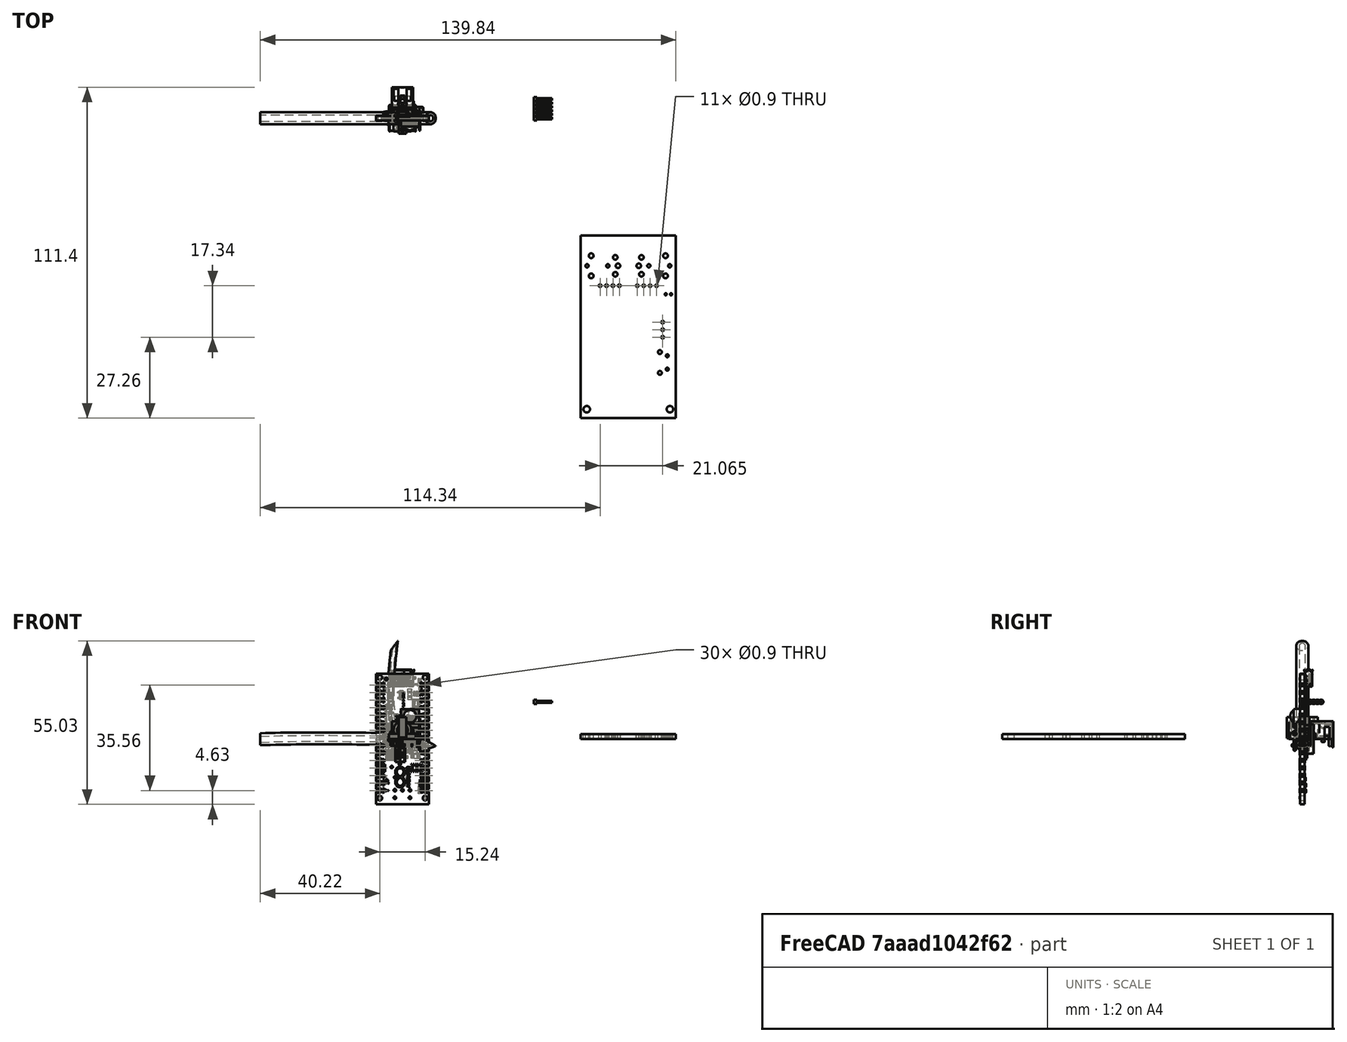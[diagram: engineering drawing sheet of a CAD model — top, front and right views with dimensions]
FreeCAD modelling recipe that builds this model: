
FCSTD DOCUMENT  (FreeCAD 0.21R33694 (Git))
Label: mainboard_step
License: All rights reserved
LicenseURL: http://en.wikipedia.org/wiki/All_rights_reserved
objects: Part::Feature×109, App::Part×72, Sketcher::SketchObject×23, PartDesign::Pad×7, PartDesign::Body×6, Part::Sweep×6, App::VRMLObject×6, Mesh::Feature×5, Image::ImagePlane×3, PartDesign::AdditivePipe×2
note: 162 computed .brp shape members not serialized (recipe doc carries the construction recipe); baked Part::Feature solids carry a one-line shape summary decoded from their .brp

FEATURE [Part::Feature] Part__Feature  label="SOLID"
  shape: bbox 1.6 x 0.8 x 0.8 mm, 28 faces (baked)
FEATURE [App::Part] C_0603_1608Metric
  Group = -> [Part__Feature]
  Origin = -> Origin
  Placement = pos=(70.4,-42.375,1.65) rot=(0,0,1;3.14159rad)
FEATURE [Part::Feature] Part__Feature001  label="SOLID001"
  shape: bbox 2.8 x 3 x 4.75 mm, 48 faces (baked)
FEATURE [App::Part] SFH4045N
  Group = -> [Part__Feature001]
  Origin = -> Origin001
  Placement = pos=(66.4,-99.3,2.24) rot=(0.57735,-0.57735,0.57735;2.0944rad)
FEATURE [Part::Feature] Part__Feature002  label="SOLID002"
  shape: bbox 2.506 x 2.463 x 1.1 mm, 67 faces (baked)
FEATURE [App::Part] D_SOD_323  label="D_SOD-323"
  Group = -> [Part__Feature002]
  Origin = -> Origin002
  Placement = pos=(74,-42.4,1.65) rot=(0,0,1;0rad)
FEATURE [Part::Feature] Part__Feature003  label="SOLID003"
  shape: bbox 1.6 x 0.8 x 0.45 mm, 26 faces (baked)
FEATURE [App::Part] R_0603_1608Metric
  Group = -> [Part__Feature003]
  Origin = -> Origin003
  Placement = pos=(86,-92.9,1.65) rot=(0,0,1;0rad)
FEATURE [Part::Feature] Part__Feature006  label="SOLID005"
  shape: bbox 1.6 x 0.8 x 0.8 mm, 28 faces (baked)
FEATURE [App::Part] C_0603_1608Metric001
  Group = -> [Part__Feature006]
  Origin = -> Origin006
  Placement = pos=(81.6,-42.4,1.65) rot=(0,0,1;0rad)
FEATURE [Part::Feature] Part__Feature008  label="SOLID007"
  shape: bbox 2.506 x 2.463 x 1.1 mm, 67 faces (baked)
FEATURE [App::Part] D_SOD_323001  label="D_SOD-324"
  Group = -> [Part__Feature008]
  Origin = -> Origin008
  Placement = pos=(78,-42.4,1.65) rot=(0,0,1;3.14159rad)
FEATURE [Part::Feature] Part__Feature010  label="SOLID008"
  shape: bbox 1.6 x 0.8 x 0.45 mm, 26 faces (baked)
FEATURE [App::Part] R_0603_1608Metric001
  Group = -> [Part__Feature010]
  Origin = -> Origin010
  Placement = pos=(82.7,-93.9,1.65) rot=(0,0,1;1.5708rad)
FEATURE [Part::Feature] Part__Feature011  label="SOLID009"
  shape: bbox 7.4 x 9.9 x 11 mm, 130 faces (baked)
FEATURE [App::Part] SW_Tactile_SPST_Angled_PTS645Vx58_2LFS  label="SW_Tactile_SPST_Angled_PTS645Vx58-2LFS"
  Group = -> [Part__Feature011]
  Origin = -> Origin011
  Placement = pos=(89.1,-80,1.9) rot=(0,0,-1;1.5708rad)
FEATURE [Part::Feature] Part__Feature012  label="SOLID010"
  shape: bbox 1.6 x 0.8 x 0.8 mm, 28 faces (baked)
FEATURE [App::Part] C_0603_1608Metric002
  Group = -> [Part__Feature012]
  Origin = -> Origin012
  Placement = pos=(71.2,-70.662,1.65) rot=(0,0,1;1.5708rad)
FEATURE [Part::Feature] Part__Feature013  label="SOLID011"
  shape: bbox 2.8 x 3 x 4.75 mm, 48 faces (baked)
FEATURE [App::Part] SFH4045N001
  Group = -> [Part__Feature013]
  Origin = -> Origin013
  Placement = pos=(90.3,-94,2.24) rot=(0.707107,0,0.707107;3.14159rad)
FEATURE [Part::Feature] Part__Feature014  label="SOLID012"
  shape: bbox 1.6 x 0.8 x 0.45 mm, 26 faces (baked)
FEATURE [App::Part] R_0603_1608Metric002
  Group = -> [Part__Feature014]
  Origin = -> Origin014
  Placement = pos=(82.7,-97.1,1.65) rot=(0,0,1;1.5708rad)
FEATURE [Part::Feature] Part__Feature015  label="SOLID013"
  shape: bbox 2.8 x 3 x 4.75 mm, 48 faces (baked)
FEATURE [App::Part] SFH4045N002
  Group = -> [Part__Feature015]
  Origin = -> Origin015
  Placement = pos=(85.6,-99.3,2.24) rot=(0.57735,-0.57735,0.57735;2.0944rad)
FEATURE [Part::Feature] Part__Feature017  label="COMPOUND003"
  shape: bbox 9.637 x 7.014 x 5.767 mm, 553 faces, 8 solids (baked)
FEATURE [App::Part] _90367280676  label="690367280676_wrl"
  Group = -> [Part__Feature017]
  Origin = -> Origin017
  Placement = pos=(75.965,-84.05,4.15) rot=(0,0,1;0rad)
FEATURE [Part::Feature] Part__Feature018  label="SOLID014"
  shape: bbox 2.8 x 3 x 4.75 mm, 48 faces (baked)
FEATURE [App::Part] SFH4045N003
  Group = -> [Part__Feature018]
  Origin = -> Origin018
  Placement = pos=(61.681,-93.2,2.24) rot=(0,-1,0;1.5708rad)
FEATURE [Part::Feature] Part__Feature020  label="SOLID015"
  shape: bbox 9 x 9 x 1.9 mm, 41 faces (baked)
FEATURE [App::Part] Buzzer_Murata_PKMCS0909E4000_R1  label="Buzzer_Murata_PKMCS0909E4000-R1"
  Group = -> [Part__Feature020]
  Origin = -> Origin020
  Placement = pos=(76.4,-62.9,1.65) rot=(0,0,1;3.14159rad)
FEATURE [Part::Feature] Part__Feature021  label="SOLID016"
  shape: bbox 3.18 x 3.679 x 1.2 mm, 76 faces (baked)
FEATURE [App::Part] SOT_23  label="SOT-23"
  Group = -> [Part__Feature021]
  Origin = -> Origin021
  Placement = pos=(86.4,-89.85,1.65) rot=(0,0,1;0rad)
FEATURE [Part::Feature] Part__Feature022  label="SOLID017"
  shape: bbox 1.6 x 0.8 x 0.8 mm, 28 faces (baked)
FEATURE [App::Part] C_0603_1608Metric003
  Group = -> [Part__Feature022]
  Origin = -> Origin022
  Placement = pos=(80.79,-70.69,1.65) rot=(0,0,1;1.5708rad)
FEATURE [Part::Feature] Part__Feature023  label="SOLID018"
  shape: bbox 3.2 x 2.5 x 2.5 mm, 28 faces (baked)
FEATURE [App::Part] C_1210_3225Metric
  Group = -> [Part__Feature023]
  Origin = -> Origin023
  Placement = pos=(82.6,-89.9,1.65) rot=(0,0,1;1.5708rad)
FEATURE [Part::Feature] Part__Feature024  label="SOLID019"
  shape: bbox 4.776 x 10.36 x 7.4 mm, 150 faces (baked)
FEATURE [App::Part] PinSocket_1x04_P2_54mm_Vertical_SMD_Pin1Right  label="PinSocket_1x04_P2.54mm_Vertical_SMD_Pin1Right"
  Group = -> [Part__Feature024]
  Origin = -> Origin024
  Placement = pos=(76,-97.1,1.65) rot=(0,0,-1;1.5708rad)
FEATURE [Part::Feature] Part__Feature025  label="SOLID020"
  shape: bbox 6 x 7.908 x 13.34 mm, 75 faces (baked)
FEATURE [App::Part] Vishay_MOLD_3Pin  label="Vishay_MOLD-3Pin"
  Group = -> [Part__Feature025]
  Origin = -> Origin025
  Placement = pos=(87.565,-73.74,0.15) rot=(0,0,1;1.5708rad)
FEATURE [Part::Feature] Part__Feature026  label="COMPOUND005"
  shape: bbox 5.019 x 5.033 x 5.871 mm, 347 faces, 24 solids (baked)
FEATURE [App::Part] Honeywell_MPRL
  Group = -> [Part__Feature026]
  Origin = -> Origin026
  Placement = pos=(76,-70.662,1.65) rot=(0,0,1;0rad)
FEATURE [Part::Feature] Part__Feature028  label="FM3_mainboard PCB"
  shape: bbox 32 x 61.5 x 1.6 mm, 39 faces (baked)
FEATURE [Image::ImagePlane] ImagePlane
  Placement = pos=(76.25,-70,3e-16) rot=(0,1,0;3.14159rad)
  XSize = 32
  YSize = 61.5
FEATURE [Image::ImagePlane] ImagePlane001
  Placement = pos=(76,-70.25,1.75) rot=(0,0,1;0rad)
  XSize = 32
  YSize = 61.5
FEATURE [Part::Feature] Part__Feature029  label="Nano_33IoT Body"
  shape: bbox 17.78 x 1.75 x 44 mm, 2561 faces (baked)
FEATURE [Part::Feature] Part__Feature030  label="User Library-arduino_nano_reset core"
  shape: bbox 5.209 x 2.159 x 2.809 mm, 76 faces (baked)
FEATURE [Part::Feature] Part__Feature031  label="User Library-arduino_nano_reset shell"
  Placement = pos=(0,1.65,0) rot=(0,-1,0;1.5708rad)
  shape: bbox 4 x 1.65 x 3 mm, 71 faces (baked)
FEATURE [App::Part] Reser_Button  label="Reser Button"
  Group = -> [Part__Feature030,Part__Feature031]
  Origin = -> Origin030
  Placement = pos=(4.5e-15,0.8,10.91) rot=(0,0,1;0rad)
FEATURE [Part::Feature] Part__Feature032  label="atmegaSAMD21"
  Placement = pos=(-1.21,0.82,-0.24) rot=(0,1,0;1.5708rad)
  shape: bbox 7.242 x 1.032 x 7.242 mm, 984 faces (baked)
FEATURE [Part::Feature] Part__Feature033  label="HSMG-C190 LED"
  Placement = pos=(5.79,0.8,19.6) rot=(0,-1,0;1.5708rad)
  shape: bbox 0.8 x 0.8 x 1.6 mm, 18 faces (baked)
FEATURE [Part::Feature] Part__Feature034  label="HSMG-C190 LED001"
  Placement = pos=(-5.81,0.8,20.1) rot=(0,-1,0;1.5708rad)
  shape: bbox 0.8 x 0.8 x 1.6 mm, 18 faces (baked)
FEATURE [Part::Feature] Part__Feature035  label="ZX62-AB-5PA Micro USB"
  Placement = pos=(0,2.22,19.2) rot=(0,0,1;0rad)
  shape: bbox 8.814 x 3.085 x 5.639 mm, 871 faces (baked)
FEATURE [Part::Feature] Part__Feature036  label="LSM6DS3 Accelerometer"
  Placement = pos=(4.6275,0.82,12) rot=(0,1,0;3.14159rad)
  shape: bbox 2.5 x 0.85 x 3 mm, 190 faces (baked)
FEATURE [Part::Feature] Part__Feature037  label="MPM3610 Step-Down Module"
  Placement = pos=(3.69,1.65,6.25) rot=(0,-1,0;1.5708rad)
  shape: bbox 5.15 x 1.65 x 3.3 mm, 330 faces (baked)
FEATURE [Part::Feature] Part__Feature038  label="NINA-W102 Body"
  shape: bbox 14 x 0.85 x 10 mm, 250 faces (baked)
FEATURE [Part::Feature] Part__Feature039  label="NINA-W102 Antenna"
  Placement = pos=(7,0.8,2e-15) rot=(0,0,1;0rad)
  shape: bbox 3.8 x 3 x 10 mm, 99 faces (baked)
FEATURE [Part::Feature] Part__Feature040  label="NINA-W102 Cover"
  Placement = pos=(-1.7,2,0) rot=(0,-1,0;1.5708rad)
  shape: bbox 9.6 x 1.45 x 9.5 mm, 75 faces (baked)
FEATURE [App::Part] NINA_W102_Module  label="NINA-W102 Module"
  Group = -> [Part__Feature038,Part__Feature039,Part__Feature040]
  Origin = -> Origin031
  Placement = pos=(2.17e-14,0.85,-14.5) rot=(0,1,0;1.5708rad)
FEATURE [Part::Feature] Part__Feature041  label="ATECC608A No Lead Crypto Auth"
  Placement = pos=(-4.035,0.8,-6.08) rot=(0,1,0;1.5708rad)
  shape: bbox 3.3 x 0.55 x 2 mm, 213 faces (baked)
FEATURE [Part::Feature] Part__Feature042  label="CL21A226MQCLQNC Capacitor"
  Placement = pos=(4.44,1.225,-5.85) rot=(0,1,0;3.14159rad)
  shape: bbox 3 x 0.8705 x 1.25 mm, 52 faces (baked)
FEATURE [Part::Feature] Part__Feature043  label="TDK C1005 Capacitor"
  Placement = pos=(5.5825,1.05,-15.55) rot=(0,1,0;1.5708rad)
  shape: bbox 0.5 x 0.5165 x 1.8 mm, 46 faces (baked)
FEATURE [Part::Feature] Part__Feature044  label="TDK C1005 Capacitor001"
  Placement = pos=(5.5825,1.05,-17.5125) rot=(0,1,0;1.5708rad)
  shape: bbox 0.5 x 0.5165 x 1.8 mm, 46 faces (baked)
FEATURE [Part::Feature] Part__Feature045  label="CL21A226MQCLQNC Capacitor001"
  Placement = pos=(-4.11,1.225,7.8375) rot=(0,-1,0;1.5708rad)
  shape: bbox 1.25 x 0.8705 x 3 mm, 52 faces (baked)
FEATURE [Part::Feature] Part__Feature046  label="TDK C1005 Capacitor002"
  Placement = pos=(5.385,1.05,15.7375) rot=(0,0,1;0rad)
  shape: bbox 1.8 x 0.5165 x 0.5 mm, 46 faces (baked)
FEATURE [Part::Feature] Part__Feature047  label="TDK C1005 Capacitor003"
  Placement = pos=(5.385,1.05,14.7625) rot=(0,0,1;0rad)
  shape: bbox 1.8 x 0.5165 x 0.5 mm, 46 faces (baked)
FEATURE [Part::Feature] Part__Feature048  label="PRTR5V0U2X Protection Diode"
  Placement = pos=(-0.41,1.45,14.77) rot=(0,1,0;1.5708rad)
  shape: bbox 2.5 x 1.1 x 3 mm, 139 faces (baked)
FEATURE [Part::Feature] Part__Feature049  label="PMEG6020AELR Diode"
  Placement = pos=(-4.06,0.85,14.1) rot=(0,-1,0;1.5708rad)
  shape: bbox 1.9 x 1.11 x 3.3 mm, 80 faces (baked)
FEATURE [Part::Feature] Part__Feature050  label="C0805C472KDRACTU Capacitor"
  Placement = pos=(2.415,1.425,15.1325) rot=(0,-1,0;1.5708rad)
  shape: bbox 1.25 x 1.301 x 3.5 mm, 52 faces (baked)
FEATURE [Part::Feature] Part__Feature051  label="TDK C1005 Capacitor004"
  Placement = pos=(-1.52,1.05,-6.46) rot=(0,1,0;1.5708rad)
  shape: bbox 0.5 x 0.5165 x 1.8 mm, 46 faces (baked)
FEATURE [Part::Feature] Part__Feature052  label="BLM18PG471SN1D Ferrite Bead"
  Placement = pos=(0.61,1.2,-6.1) rot=(0,1,0;3.14159rad)
  shape: bbox 2.5 x 0.8142 x 0.8 mm, 52 faces (baked)
FEATURE [Part::Feature] Part__Feature053  label="TDK C1005 Capacitor005"
  Placement = pos=(-5.66,1.05,-4.35) rot=(0,1,0;3.14159rad)
  shape: bbox 1.8 x 0.5165 x 0.5 mm, 46 faces (baked)
FEATURE [Part::Feature] Part__Feature054  label="TDK C1005 Capacitor006"
  Placement = pos=(-3.64,1.05,10.73) rot=(0,-1,0;1.5708rad)
  shape: bbox 0.5 x 0.5165 x 1.8 mm, 46 faces (baked)
FEATURE [Part::Feature] Part__Feature055  label="TDK C1005 Capacitor007"
  Placement = pos=(-3.79,1.05,5.1) rot=(0,0,1;0rad)
  shape: bbox 1.8 x 0.5165 x 0.5 mm, 46 faces (baked)
FEATURE [Part::Feature] Part__Feature056  label="GRM188R61E475KE11D Capacitor"
  Placement = pos=(-5.59,1.2,4.4) rot=(0,-1,0;1.5708rad)
  shape: bbox 0.8 x 0.8142 x 2.5 mm, 52 faces (baked)
FEATURE [Part::Feature] Part__Feature057  label="RC0402FR-07100KL Resistor"
  Placement = pos=(-2.01,1,8.1625) rot=(0,1,0;3.14159rad)
  shape: bbox 1.47 x 0.4379 x 0.5 mm, 68 faces (baked)
FEATURE [Part::Feature] Part__Feature058  label="RC0402FR-07100KL Resistor001"
  Placement = pos=(-1.6975,1,6.7125) rot=(0,-1,0;1.5708rad)
  shape: bbox 0.5 x 0.4379 x 1.47 mm, 68 faces (baked)
FEATURE [Part::Feature] Part__Feature059  label="RC0402FR-07330RL Resistor"
  Placement = pos=(-5.81,1,16.6) rot=(0,-1,0;1.5708rad)
  shape: bbox 0.5 x 0.4379 x 1.47 mm, 68 faces (baked)
FEATURE [Part::Feature] Part__Feature060  label="RC0402FR-07330RL Resistor001"
  Placement = pos=(5.8025,1,17.2) rot=(0,-1,0;1.5708rad)
  shape: bbox 0.5 x 0.4379 x 1.47 mm, 68 faces (baked)
FEATURE [Part::Feature] Part__Feature061  label="RC0402FR-07330RL Resistor002"
  Placement = pos=(3.915,1,15.2325) rot=(0,-1,0;1.5708rad)
  shape: bbox 0.5 x 0.4379 x 1.47 mm, 68 faces (baked)
FEATURE [Part::Feature] Part__Feature062  label="TDK C1005 Capacitor008"
  Placement = pos=(5.09,1.05,3.1) rot=(0,1,0;3.14159rad)
  shape: bbox 1.8 x 0.5165 x 0.5 mm, 46 faces (baked)
FEATURE [Part::Feature] Part__Feature063  label="RC0402FR-074K7L Resistor"
  Placement = pos=(5.09,1,2.1) rot=(0,0,1;0rad)
  shape: bbox 1.47 x 0.4379 x 0.5 mm, 68 faces (baked)
FEATURE [Part::Feature] Part__Feature064  label="RC0402FR-074K7L Resistor001"
  Placement = pos=(5.09,1,1.1) rot=(0,1,0;3.14159rad)
  shape: bbox 1.47 x 0.4379 x 0.5 mm, 68 faces (baked)
FEATURE [Part::Feature] Part__Feature065  label="GRM155R61E105KA12D Capacitor"
  Placement = pos=(5.09,1.05,0.1) rot=(0,0,1;0rad)
  shape: bbox 1.8 x 0.5165 x 0.5 mm, 46 faces (baked)
FEATURE [Part::Feature] Part__Feature066  label="TDK C1005 Capacitor009"
  Placement = pos=(5.09,1.05,-0.9) rot=(0,1,0;3.14159rad)
  shape: bbox 1.8 x 0.5165 x 0.5 mm, 46 faces (baked)
FEATURE [Part::Feature] Part__Feature067  label="RC0402FR-071KL Resistor"
  Placement = pos=(5.09,1,-1.9) rot=(0,1,0;3.14159rad)
  shape: bbox 1.47 x 0.4379 x 0.5 mm, 68 faces (baked)
FEATURE [Part::Feature] Part__Feature068  label="RC0402FR-07100KL Resistor002"
  Placement = pos=(-5.74,1,-13.5) rot=(0,1,0;1.5708rad)
  shape: bbox 0.5 x 0.4379 x 1.47 mm, 68 faces (baked)
FEATURE [Part::Feature] Part__Feature069  label="RC0402FR-07100KL Resistor003"
  Placement = pos=(-4.64,1,10.73) rot=(0,-1,0;1.5708rad)
  shape: bbox 0.5 x 0.4379 x 1.47 mm, 68 faces (baked)
FEATURE [Part::Feature] Part__Feature070  label="AC0402JR-0724KL Resistor"
  Placement = pos=(4.665,0.985,9.725) rot=(0,0,1;0rad)
  shape: bbox 1.47 x 0.4079 x 0.5 mm, 68 faces (baked)
FEATURE [Part::Feature] Part__Feature071  label="AC0402JR-0775KL Resistor"
  Placement = pos=(4.665,0.985,8.725) rot=(0,0,1;0rad)
  shape: bbox 1.47 x 0.4079 x 0.5 mm, 68 faces (baked)
FEATURE [App::Part] Arduino_Nano_33_IoT  label="Arduino Nano 33 IoT"
  Group = -> [Part__Feature029,Reser_Button,Part__Feature032,Part__Feature033,Part__Feature034,Part__Feature035,Part__Feature036,Part__Feature037,NINA_W102_Module,Part__Feature041,Part__Feature042,Part__Feature043,Part__Feature044,Part__Feature045,Part__Feature046,Part__Feature047,Part__Feature048,Part__Feature049,Part__Feature050,Part__Feature051,Part__Feature052,Part__Feature053,Part__Feature054,+17 more]
  Origin = -> Origin032
FEATURE [App::Part] ArduinoNanoRP2040
  Group = -> [Arduino_Nano_33_IoT]
  Origin = -> Origin027
  Placement = pos=(73.4,-78.1,-0.05) rot=(0,0.707107,-0.707107;3.14159rad)
FEATURE [Part::Feature] Part__Feature072  label="Telo konektora"
  shape: bbox 7 x 14.9 x 7.247 mm, 88 faces (baked)
FEATURE [Part::Feature] Part__Feature073  label="Kontakt most"
  shape: bbox 7.472 x 8.966 x 8.306 mm, 60 faces (baked)
FEATURE [Part::Feature] Part__Feature074  label="Kontakt 1"
  shape: bbox 6 x 4 x 8.5 mm, 26 faces, 2 solids (baked)
FEATURE [Part::Feature] Part__Feature075  label="Kontakt 2"
  shape: bbox 1 x 0.3 x 3 mm, 8 faces (baked)
FEATURE [App::Part] Audio_konektor_FC68125_3_5_mm_v5  label="Audio konektor FC68125 3.5 mm v5"
  Group = -> [Part__Feature072,Part__Feature073,Part__Feature074,Part__Feature075]
  Origin = -> Origin033
FEATURE [App::Part] FC68125
  Group = -> [Audio_konektor_FC68125_3_5_mm_v5]
  Origin = -> Origin004
  Placement = pos=(62.4,-49.7,1.65) rot=(0,0,-1;1.5708rad)
FEATURE [Part::Feature] Part__Feature076  label="Telo konektora001"
  shape: bbox 7 x 14.9 x 7.247 mm, 88 faces (baked)
FEATURE [Part::Feature] Part__Feature077  label="Kontakt most001"
  shape: bbox 7.472 x 8.966 x 8.306 mm, 60 faces (baked)
FEATURE [Part::Feature] Part__Feature078  label="Kontakt 003"
  shape: bbox 6 x 4 x 8.5 mm, 26 faces, 2 solids (baked)
FEATURE [Part::Feature] Part__Feature079  label="Kontakt 004"
  shape: bbox 1 x 0.3 x 3 mm, 8 faces (baked)
FEATURE [App::Part] Audio_konektor_FC68125_3_5_mm_v006  label="Audio konektor FC68125 3.5 mm v006"
  Group = -> [Part__Feature076,Part__Feature077,Part__Feature078,Part__Feature079]
  Origin = -> Origin034
FEATURE [App::Part] FC68125001
  Group = -> [Audio_konektor_FC68125_3_5_mm_v006]
  Origin = -> Origin016
  Placement = pos=(89.6,-49.7,1.65) rot=(0,0,1;1.5708rad)
FEATURE [Mesh::Feature] np_led_bendlegs
FEATURE [App::Part] LED_D5_0mm_Horizontal_O3_81mm_Z9_0mm001  label="LED_D5.0mm_Horizontal_O3.81mm_Z9.0mm001"
  Group = -> [np_led_bendlegs]
  Origin = -> Origin007
  Placement = pos=(68.5,-55.9,13.9) rot=(1,0,0;3.14159rad)
FEATURE [Mesh::Feature] np_led_bendlegs001
FEATURE [App::Part] LED_D5_0mm_Horizontal_O3_81mm_Z9_0mm  label="LED_D5.0mm_Horizontal_O3.81mm_Z9.0mm"
  Group = -> [np_led_bendlegs001]
  Origin = -> Origin005
  Placement = pos=(81.023,-55.9,13.9) rot=(-1,0,0;3.14159rad)
FEATURE [Mesh::Feature] FM3_case_lid  label="FM3_case-lid"
FEATURE [Sketcher::SketchObject] Sketch
  FullyConstrained = false
  MapMode = 5
  Placement = pos=(0,0,0) rot=(0.57735,0.57735,0.57735;2.0944rad)
  sketch-geometry (23):
    g0: LineSegment StartX=0 StartY=0 StartZ=0 EndX=1.27335 EndY=0 EndZ=0
    g1: LineSegment StartX=0 StartY=0 StartZ=0 EndX=1.27103 EndY=0 EndZ=0
    g2: LineSegment StartX=1.27103 StartY=0 StartZ=0 EndX=2.54207 EndY=0 EndZ=0
    g3: LineSegment StartX=2.54207 StartY=0 StartZ=0 EndX=3.8131 EndY=0 EndZ=0
    g4: LineSegment StartX=3.8131 StartY=0 StartZ=0 EndX=5.08414 EndY=0 EndZ=0
    g5: LineSegment StartX=0.45 StartY=0.6 StartZ=0 EndX=0.821034 EndY=0.6 EndZ=0
    g6: LineSegment StartX=0.45 StartY=-0.6 StartZ=0 EndX=0.821034 EndY=-0.6 EndZ=0
    g7: ArcOfCircle CenterX=5.08414 CenterY=7.1e-15 CenterZ=0 NormalX=0 NormalY=0 NormalZ=1 AngleXU=0 Radius=0.75 StartAngle=4.06889 EndAngle=5.35589
    g8: ArcOfCircle CenterX=3.8131 CenterY=0 CenterZ=0 NormalX=0 NormalY=0 NormalZ=1 AngleXU=0 Radius=0.75 StartAngle=4.06889 EndAngle=5.35589
    g9: ArcOfCircle CenterX=2.54207 CenterY=0 CenterZ=0 NormalX=0 NormalY=0 NormalZ=1 AngleXU=0 Radius=0.75 StartAngle=4.06889 EndAngle=5.35589
    g10: ArcOfCircle CenterX=1.27103 CenterY=-2e-16 CenterZ=0 NormalX=0 NormalY=0 NormalZ=1 AngleXU=0 Radius=0.75 StartAngle=4.06889 EndAngle=5.35589
    g11: ArcOfCircle CenterX=0 CenterY=-1e-16 CenterZ=0 NormalX=0 NormalY=0 NormalZ=1 AngleXU=0 Radius=0.75 StartAngle=0.927295 EndAngle=5.35589
    g12: ArcOfCircle CenterX=1.27103 CenterY=0 CenterZ=0 NormalX=0 NormalY=0 NormalZ=1 AngleXU=0 Radius=0.75 StartAngle=0.927295 EndAngle=2.2143
    g13: ArcOfCircle CenterX=2.54207 CenterY=0 CenterZ=0 NormalX=0 NormalY=0 NormalZ=1 AngleXU=0 Radius=0.75 StartAngle=0.927295 EndAngle=2.2143
    g14: ArcOfCircle CenterX=3.8131 CenterY=0 CenterZ=0 NormalX=0 NormalY=0 NormalZ=1 AngleXU=0 Radius=0.75 StartAngle=0.927295 EndAngle=2.2143
    g15: ArcOfCircle CenterX=5.08414 CenterY=-9.81007e-08 CenterZ=0 NormalX=0 NormalY=0 NormalZ=1 AngleXU=0 Radius=0.75 StartAngle=0.927295 EndAngle=2.2143
    g16: LineSegment StartX=4.2631 StartY=0.6 StartZ=0 EndX=4.63414 EndY=0.6 EndZ=0
    g17: LineSegment StartX=2.99207 StartY=0.6 StartZ=0 EndX=3.3631 EndY=0.6 EndZ=0
    g18: LineSegment StartX=1.72103 StartY=0.6 StartZ=0 EndX=2.09207 EndY=0.6 EndZ=0
    g19: LineSegment StartX=1.72103 StartY=-0.6 StartZ=0 EndX=2.09207 EndY=-0.6 EndZ=0
    g20: LineSegment StartX=2.99207 StartY=-0.6 StartZ=0 EndX=3.3631 EndY=-0.6 EndZ=0
    g21: LineSegment StartX=4.2631 StartY=-0.6 StartZ=0 EndX=4.63414 EndY=-0.6 EndZ=0
    g22: ArcOfCircle CenterX=5.08414 CenterY=7.1e-15 CenterZ=0 NormalX=0 NormalY=0 NormalZ=1 AngleXU=0 Radius=0.75 StartAngle=5.35589 EndAngle=7.21048
  constraints (36):
    c: Angle(g0) = 0
    c: Distance(g1) = 1.27103
    c: Angle(g1) = 0
    c: Equal(g1,g2)
    c: Parallel(g2,g1)
    c: Equal(g1,g3)
    c: Parallel(g3,g1)
    c: Equal(g1,g4)
    c: Parallel(g4,g1)
    c: Horizontal(g5)
    c: Horizontal(g6)
    c: PointOnObject(g7,g6)
    c: PointOnObject(g7,g6)
    c: PointOnObject(g8,g6)
    c: PointOnObject(g8,g6)
    c: PointOnObject(g9,g6)
    c: PointOnObject(g9,g6)
    c: Coincident(g6,g11)
    c: Coincident(g11,g5)
    c: Coincident(g16,g15)
    c: Coincident(g17,g14)
    c: Coincident(g16,g14)
    c: Coincident(g18,g13)
    c: Coincident(g17,g13)
    c: Coincident(g5,g12)
    c: Coincident(g18,g12)
    c: Coincident(g6,g10)
    c: Coincident(g19,g10)
    c: PointOnObject(g19,g9)
    c: PointOnObject(g20,g9)
    c: PointOnObject(g20,g8)
    c: PointOnObject(g21,g8)
    c: PointOnObject(g21,g7)
    c: Coincident(g22,g7)
    c: Coincident(g22,g15)
    c: Coincident(g22,g7)
FEATURE [Sketcher::SketchObject] Sketch001
  FullyConstrained = false
  MapMode = 5
  Placement = pos=(0,0,0) rot=(0.57735,0.57735,0.57735;2.0944rad)
  Support = -> [YZ_Plane061]
  sketch-geometry (11):
    g0: Circle CenterX=0 CenterY=0 CenterZ=0 NormalX=0 NormalY=0 NormalZ=1 AngleXU=0 Radius=0.340608
    g1: Circle CenterX=1.26883 CenterY=0 CenterZ=0 NormalX=0 NormalY=0 NormalZ=1 AngleXU=0 Radius=0.340608
    g2: LineSegment StartX=0 StartY=0 StartZ=0 EndX=1.26883 EndY=0 EndZ=0
    g3: Circle CenterX=2.53767 CenterY=0 CenterZ=0 NormalX=0 NormalY=0 NormalZ=1 AngleXU=0 Radius=0.340608
    g4: LineSegment StartX=1.26883 StartY=0 StartZ=0 EndX=2.53767 EndY=0 EndZ=0
    g5: Circle CenterX=3.8065 CenterY=0 CenterZ=0 NormalX=0 NormalY=0 NormalZ=1 AngleXU=0 Radius=0.340608
    g6: LineSegment StartX=2.53767 StartY=0 StartZ=0 EndX=3.8065 EndY=0 EndZ=0
    g7: Circle CenterX=5.07533 CenterY=0 CenterZ=0 NormalX=0 NormalY=0 NormalZ=1 AngleXU=0 Radius=0.340608
    g8: LineSegment StartX=3.8065 StartY=0 StartZ=0 EndX=5.07533 EndY=0 EndZ=0
    g9: Circle CenterX=6.34417 CenterY=0 CenterZ=0 NormalX=0 NormalY=0 NormalZ=1 AngleXU=0 Radius=0.340608
    g10: LineSegment StartX=5.07533 StartY=0 StartZ=0 EndX=6.34417 EndY=0 EndZ=0
  constraints (21):
    c: Coincident(g0,g-1)
    c: Coincident(g0,g2)
    c: Coincident(g1,g2)
    c: Distance(g2) = 1.26883
    c: Angle(g2) = 0
    c: Coincident(g1,g4)
    c: Coincident(g3,g4)
    c: Equal(g2,g4)
    c: Parallel(g4,g2)
    c: Coincident(g3,g6)
    c: Coincident(g5,g6)
    c: Equal(g2,g6)
    c: Parallel(g6,g2)
    c: Coincident(g5,g8)
    c: Coincident(g7,g8)
    c: Equal(g2,g8)
    c: Parallel(g8,g2)
    c: Coincident(g7,g10)
    c: Coincident(g9,g10)
    c: Equal(g2,g10)
    c: Parallel(g10,g2)
FEATURE [Sketcher::SketchObject] Sketch003
  FullyConstrained = false
  MapMode = 5
  Placement = pos=(0,0,0) rot=(1,0,0;1.5708rad)
  sketch-geometry (11):
    g0-g5: Circle x6 (B-spline internal-alignment scaffolding for g6; pole/knot coordinates omitted)
    g6: BSplineCurve PolesCount=6 KnotsCount=4 Degree=3 IsPeriodic=0
    g7-g10: GeomPoint x4 (B-spline internal-alignment scaffolding for g6; pole/knot coordinates omitted)
  constraints (4):
    c: Weight(g0) = 1
    c: Equal(g0, g1-g5) x5
    c: InternalAlignment(g0-g5 -> g6) x6
    c: InternalAlignment(g7-g10 -> g6) x4
FEATURE [Sketcher::SketchObject] Sketch004
  FullyConstrained = false
  MapMode = 5
  Placement = pos=(0,0,0) rot=(0.57735,0.57735,0.57735;2.0944rad)
  sketch-geometry (26):
    g0: LineSegment StartX=0 StartY=0 StartZ=0 EndX=1.27335 EndY=0 EndZ=0
    g1: LineSegment StartX=0 StartY=0 StartZ=0 EndX=1.27103 EndY=0 EndZ=0
    g2: LineSegment StartX=1.27103 StartY=0 StartZ=0 EndX=2.54207 EndY=0 EndZ=0
    g3: LineSegment StartX=2.54207 StartY=0 StartZ=0 EndX=3.8131 EndY=0 EndZ=0
    g4: LineSegment StartX=3.8131 StartY=0 StartZ=0 EndX=5.08414 EndY=0 EndZ=0
    g5: ArcOfCircle CenterX=6.35517 CenterY=0 CenterZ=0 NormalX=0 NormalY=0 NormalZ=1 AngleXU=0 Radius=0.75 StartAngle=4.06889 EndAngle=8.49748
    g6: LineSegment StartX=5.08414 StartY=0 StartZ=0 EndX=6.35517 EndY=0 EndZ=0
    g7: LineSegment StartX=0.45 StartY=0.6 StartZ=0 EndX=0.821034 EndY=0.6 EndZ=0
    g8: LineSegment StartX=0.45 StartY=-0.6 StartZ=0 EndX=0.821034 EndY=-0.6 EndZ=0
    g9: ArcOfCircle CenterX=5.08414 CenterY=0 CenterZ=0 NormalX=0 NormalY=0 NormalZ=1 AngleXU=0 Radius=0.75 StartAngle=4.06889 EndAngle=5.35589
    g10: ArcOfCircle CenterX=3.8131 CenterY=0 CenterZ=0 NormalX=0 NormalY=0 NormalZ=1 AngleXU=0 Radius=0.75 StartAngle=4.06889 EndAngle=5.35589
    g11: ArcOfCircle CenterX=2.54207 CenterY=0 CenterZ=0 NormalX=0 NormalY=0 NormalZ=1 AngleXU=0 Radius=0.75 StartAngle=4.06889 EndAngle=5.35589
    g12: ArcOfCircle CenterX=1.27103 CenterY=0 CenterZ=0 NormalX=0 NormalY=0 NormalZ=1 AngleXU=0 Radius=0.75 StartAngle=4.06889 EndAngle=5.35589
    g13: ArcOfCircle CenterX=0 CenterY=0 CenterZ=0 NormalX=0 NormalY=0 NormalZ=1 AngleXU=0 Radius=0.75 StartAngle=0.927295 EndAngle=5.35589
    g14: ArcOfCircle CenterX=1.27103 CenterY=0 CenterZ=0 NormalX=0 NormalY=0 NormalZ=1 AngleXU=0 Radius=0.75 StartAngle=0.927295 EndAngle=2.2143
    g15: ArcOfCircle CenterX=2.54207 CenterY=0 CenterZ=0 NormalX=0 NormalY=0 NormalZ=1 AngleXU=0 Radius=0.75 StartAngle=0.927295 EndAngle=2.2143
    g16: ArcOfCircle CenterX=3.8131 CenterY=0 CenterZ=0 NormalX=0 NormalY=0 NormalZ=1 AngleXU=0 Radius=0.75 StartAngle=0.927295 EndAngle=2.2143
    g17: ArcOfCircle CenterX=5.08414 CenterY=0 CenterZ=0 NormalX=0 NormalY=0 NormalZ=1 AngleXU=0 Radius=0.75 StartAngle=0.927295 EndAngle=2.2143
    g18: LineSegment StartX=5.53414 StartY=0.6 StartZ=0 EndX=5.90517 EndY=0.6 EndZ=0
    g19: LineSegment StartX=4.2631 StartY=0.6 StartZ=0 EndX=4.63414 EndY=0.6 EndZ=0
    g20: LineSegment StartX=2.99207 StartY=0.6 StartZ=0 EndX=3.3631 EndY=0.6 EndZ=0
    g21: LineSegment StartX=1.72103 StartY=0.6 StartZ=0 EndX=2.09207 EndY=0.6 EndZ=0
    g22: LineSegment StartX=1.72103 StartY=-0.6 StartZ=0 EndX=2.09207 EndY=-0.6 EndZ=0
    g23: LineSegment StartX=2.99207 StartY=-0.6 StartZ=0 EndX=3.3631 EndY=-0.6 EndZ=0
    g24: LineSegment StartX=4.2631 StartY=-0.6 StartZ=0 EndX=4.63414 EndY=-0.6 EndZ=0
    g25: LineSegment StartX=5.53414 StartY=-0.6 StartZ=0 EndX=5.90517 EndY=-0.6 EndZ=0
  constraints (41):
    c: Angle(g0) = 0
    c: Distance(g1) = 1.27103
    c: Angle(g1) = 0
    c: Equal(g1,g2)
    c: Parallel(g2,g1)
    c: Equal(g1,g3)
    c: Parallel(g3,g1)
    c: Equal(g1,g4)
    c: Parallel(g4,g1)
    c: Radius(g5) = 0.75
    c: Coincident(g5,g6)
    c: Equal(g1,g6)
    c: Parallel(g6,g1)
    c: Horizontal(g7)
    c: Horizontal(g8)
    c: Coincident(g5,g25)
    c: PointOnObject(g9,g8)
    c: PointOnObject(g9,g8)
    c: PointOnObject(g10,g8)
    c: PointOnObject(g10,g8)
    c: PointOnObject(g11,g8)
    c: PointOnObject(g11,g8)
    c: Coincident(g8,g13)
    c: Coincident(g13,g7)
    c: Coincident(g18,g5)
    c: Coincident(g19,g17)
    c: Coincident(g18,g17)
    c: Coincident(g20,g16)
    c: Coincident(g19,g16)
    c: Coincident(g21,g15)
    c: Coincident(g20,g15)
    c: Coincident(g7,g14)
    c: Coincident(g21,g14)
    c: Coincident(g8,g12)
    c: Coincident(g22,g12)
    c: PointOnObject(g22,g11)
    c: PointOnObject(g23,g11)
    c: PointOnObject(g23,g10)
    c: PointOnObject(g24,g10)
    c: PointOnObject(g24,g9)
    c: PointOnObject(g25,g9)
FEATURE [PartDesign::Pad] Pad
  Direction = (1,0,0)
  Length = 1
  Length2 = 10
  Placement = pos=(0,0,0) rot=(0.57735,0.57735,0.57735;2.0944rad)
  Profile = -> Sketch004
  ReferenceAxis = -> Sketch004 [N_Axis]
  Type = 0
FEATURE [PartDesign::Pad] Pad001
  BaseFeature = -> Pad
  Direction = (1,-2e-16,3e-16)
  Length = 6
  Length2 = 10
  Placement = pos=(0,0,0) rot=(0.57735,0.57735,0.57735;2.0944rad)
  Profile = -> Sketch001
  ReferenceAxis = -> Sketch001 [N_Axis]
  Type = 0
FEATURE [PartDesign::Body] Body001
  Group = -> [Sketch001,Sketch004,Pad,Pad001]
  Origin = -> Origin061
  Placement = pos=(44.25,0,12.5) rot=(0,0,1;0rad)
  Tip = -> Pad001
FEATURE [Sketcher::SketchObject] Sketch005
  FullyConstrained = false
  MapMode = 5
  Placement = pos=(0,0,0) rot=(0.57735,0.57735,0.57735;2.0944rad)
  sketch-geometry (2):
    g0: ArcOfCircle CenterX=6.35517 CenterY=-2.69756e-08 CenterZ=0 NormalX=0 NormalY=0 NormalZ=1 AngleXU=0 Radius=0.75 StartAngle=4.06889 EndAngle=8.49748
    g1: ArcOfCircle CenterX=6.35517 CenterY=-2.69756e-08 CenterZ=0 NormalX=0 NormalY=0 NormalZ=1 AngleXU=0 Radius=0.75 StartAngle=2.2143 EndAngle=4.06889
  constraints (4):
    c: Radius(g0) = 0.75
    c: Coincident(g1,g0)
    c: Coincident(g1,g0)
    c: Coincident(g1,g0)
FEATURE [Sketcher::SketchObject] Sketch006
  FullyConstrained = false
  MapMode = 5
  Placement = pos=(0,0,0) rot=(1,0,0;1.5708rad)
  sketch-geometry (11):
    g0-g5: Circle x6 (B-spline internal-alignment scaffolding for g6; pole/knot coordinates omitted)
    g6: BSplineCurve PolesCount=6 KnotsCount=4 Degree=3 IsPeriodic=0
    g7-g10: GeomPoint x4 (B-spline internal-alignment scaffolding for g6; pole/knot coordinates omitted)
  constraints (4):
    c: Weight(g0) = 1
    c: Equal(g0, g1-g5) x5
    c: InternalAlignment(g0-g5 -> g6) x6
    c: InternalAlignment(g7-g10 -> g6) x4
FEATURE [Part::Sweep] Sweep
  Frenet = false
  Sections = -> [Sketch]
  Solid = false
  Spine = -> Sketch003 [Edge1]
  Transition = 1
FEATURE [Part::Sweep] Sweep001
  Frenet = false
  Sections = -> [Sketch005]
  Solid = false
  Spine = -> Sketch006 [Edge1]
  Transition = 1
FEATURE [App::Part] Part003  label="idc-cable_mounted"
  Group = -> [Body001,Sketch003,Sketch,Sweep,Sketch005,Sketch006,Sweep001]
  Origin = -> Origin062
  Placement = pos=(-3,-1.25,50.25) rot=(-0.57735,-0.57735,0.57735;4.18879rad)
FEATURE [App::VRMLObject] _90157000672001  label="690157000672001"
FEATURE [App::Part] Part004  label="idc-plug_mounted"
  Group = -> [_90157000672001]
  Origin = -> Origin063
  Placement = pos=(-2.18e-14,-0.5,53) rot=(1,0,0;4.71239rad)
FEATURE [Sketcher::SketchObject] Sketch007
  FullyConstrained = true
  MapMode = 5
  Placement = pos=(0,0,0) rot=(0.57735,0.57735,0.57735;2.0944rad)
  Support = -> [YZ_Plane066]
  sketch-geometry (2):
    g0: Circle CenterX=0 CenterY=0 CenterZ=0 NormalX=0 NormalY=0 NormalZ=1 AngleXU=0 Radius=2
    g1: Circle CenterX=0 CenterY=0 CenterZ=0 NormalX=0 NormalY=0 NormalZ=1 AngleXU=0 Radius=3
  constraints (4):
    c: Coincident(g0,g-1)
    c: Radius(g0) = 2
    c: Coincident(g1,g0)
    c: Radius(g1) = 3
FEATURE [PartDesign::Pad] Pad002
  Direction = (1,-2e-16,3e-16)
  Length = 5
  Length2 = 10
  Placement = pos=(0,0,0) rot=(0.57735,0.57735,0.57735;2.0944rad)
  Profile = -> Sketch007
  ReferenceAxis = -> Sketch007 [N_Axis]
  Type = 0
FEATURE [PartDesign::Body] Body  label="4x6_5mm"
  Group = -> [Sketch007,Pad002]
  Origin = -> Origin066
  Tip = -> Pad002
FEATURE [Sketcher::SketchObject] Sketch008  label="diameter"
  FullyConstrained = true
  MapMode = 5
  Placement = pos=(0,0,0) rot=(0.57735,0.57735,0.57735;2.0944rad)
  Support = -> [YZ_Plane067]
  sketch-geometry (2):
    g0: Circle CenterX=0 CenterY=0 CenterZ=0 NormalX=0 NormalY=0 NormalZ=1 AngleXU=0 Radius=1
    g1: Circle CenterX=0 CenterY=0 CenterZ=0 NormalX=0 NormalY=0 NormalZ=1 AngleXU=0 Radius=2
  constraints (4):
    c: Coincident(g0,g-1)
    c: Radius(g0) = 1
    c: Coincident(g1,g0)
    c: Radius(g1) = 2
FEATURE [Sketcher::SketchObject] Sketch009  label="sweep"
  FullyConstrained = false
  MapMode = 5
  Placement = pos=(0,0,0) rot=(1,0,0;1.5708rad)
  Support = -> [XZ_Plane067]
  sketch-geometry (7):
    g0-g3: Circle x4 (B-spline internal-alignment scaffolding for g4; pole/knot coordinates omitted)
    g4: BSplineCurve PolesCount=4 KnotsCount=2 Degree=3 IsPeriodic=0
    g5: GeomPoint X=5.97738 Y=0.542931 Z=0
    g6: GeomPoint X=-0.39634 Y=34.6329 Z=0
  constraints (7):
    c: Weight(g0) = 1
    c: Equal(g0,g1)
    c: Equal(g0,g2)
    c: Equal(g0,g3)
    c: InternalAlignment(g0-g3 -> g4) x4
    c: InternalAlignment(g5,g4)
    c: InternalAlignment(g6,g4)
FEATURE [Sketcher::SketchObject] Sketch010
  FullyConstrained = false
  MapMode = 5
  Placement = pos=(0,0,0) rot=(0.57735,0.57735,0.57735;2.0944rad)
  sketch-geometry (23):
    g0: LineSegment StartX=0 StartY=0 StartZ=0 EndX=1.27335 EndY=0 EndZ=0
    g1: LineSegment StartX=0 StartY=0 StartZ=0 EndX=1.27103 EndY=0 EndZ=0
    g2: LineSegment StartX=1.27103 StartY=0 StartZ=0 EndX=2.54207 EndY=0 EndZ=0
    g3: LineSegment StartX=2.54207 StartY=0 StartZ=0 EndX=3.8131 EndY=0 EndZ=0
    g4: LineSegment StartX=3.8131 StartY=0 StartZ=0 EndX=5.08414 EndY=0 EndZ=0
    g5: LineSegment StartX=0.45 StartY=0.6 StartZ=0 EndX=0.821034 EndY=0.6 EndZ=0
    g6: LineSegment StartX=0.45 StartY=-0.6 StartZ=0 EndX=0.821034 EndY=-0.6 EndZ=0
    g7: ArcOfCircle CenterX=5.08414 CenterY=7.1e-15 CenterZ=0 NormalX=0 NormalY=0 NormalZ=1 AngleXU=0 Radius=0.75 StartAngle=4.06889 EndAngle=5.35589
    g8: ArcOfCircle CenterX=3.8131 CenterY=0 CenterZ=0 NormalX=0 NormalY=0 NormalZ=1 AngleXU=0 Radius=0.75 StartAngle=4.06889 EndAngle=5.35589
    g9: ArcOfCircle CenterX=2.54207 CenterY=0 CenterZ=0 NormalX=0 NormalY=0 NormalZ=1 AngleXU=0 Radius=0.75 StartAngle=4.06889 EndAngle=5.35589
    g10: ArcOfCircle CenterX=1.27103 CenterY=-2e-16 CenterZ=0 NormalX=0 NormalY=0 NormalZ=1 AngleXU=0 Radius=0.75 StartAngle=4.06889 EndAngle=5.35589
    g11: ArcOfCircle CenterX=0 CenterY=-1e-16 CenterZ=0 NormalX=0 NormalY=0 NormalZ=1 AngleXU=0 Radius=0.75 StartAngle=0.927295 EndAngle=5.35589
    g12: ArcOfCircle CenterX=1.27103 CenterY=0 CenterZ=0 NormalX=0 NormalY=0 NormalZ=1 AngleXU=0 Radius=0.75 StartAngle=0.927295 EndAngle=2.2143
    g13: ArcOfCircle CenterX=2.54207 CenterY=0 CenterZ=0 NormalX=0 NormalY=0 NormalZ=1 AngleXU=0 Radius=0.75 StartAngle=0.927295 EndAngle=2.2143
    g14: ArcOfCircle CenterX=3.8131 CenterY=0 CenterZ=0 NormalX=0 NormalY=0 NormalZ=1 AngleXU=0 Radius=0.75 StartAngle=0.927295 EndAngle=2.2143
    g15: ArcOfCircle CenterX=5.08414 CenterY=-9.81007e-08 CenterZ=0 NormalX=0 NormalY=0 NormalZ=1 AngleXU=0 Radius=0.75 StartAngle=0.927295 EndAngle=2.2143
    g16: LineSegment StartX=4.2631 StartY=0.6 StartZ=0 EndX=4.63414 EndY=0.6 EndZ=0
    g17: LineSegment StartX=2.99207 StartY=0.6 StartZ=0 EndX=3.3631 EndY=0.6 EndZ=0
    g18: LineSegment StartX=1.72103 StartY=0.6 StartZ=0 EndX=2.09207 EndY=0.6 EndZ=0
    g19: LineSegment StartX=1.72103 StartY=-0.6 StartZ=0 EndX=2.09207 EndY=-0.6 EndZ=0
    g20: LineSegment StartX=2.99207 StartY=-0.6 StartZ=0 EndX=3.3631 EndY=-0.6 EndZ=0
    g21: LineSegment StartX=4.2631 StartY=-0.6 StartZ=0 EndX=4.63414 EndY=-0.6 EndZ=0
    g22: ArcOfCircle CenterX=5.08414 CenterY=7.1e-15 CenterZ=0 NormalX=0 NormalY=0 NormalZ=1 AngleXU=0 Radius=0.75 StartAngle=5.35589 EndAngle=7.21048
  constraints (36):
    c: Angle(g0) = 0
    c: Distance(g1) = 1.27103
    c: Angle(g1) = 0
    c: Equal(g1,g2)
    c: Parallel(g2,g1)
    c: Equal(g1,g3)
    c: Parallel(g3,g1)
    c: Equal(g1,g4)
    c: Parallel(g4,g1)
    c: Horizontal(g5)
    c: Horizontal(g6)
    c: PointOnObject(g7,g6)
    c: PointOnObject(g7,g6)
    c: PointOnObject(g8,g6)
    c: PointOnObject(g8,g6)
    c: PointOnObject(g9,g6)
    c: PointOnObject(g9,g6)
    c: Coincident(g6,g11)
    c: Coincident(g11,g5)
    c: Coincident(g16,g15)
    c: Coincident(g17,g14)
    c: Coincident(g16,g14)
    c: Coincident(g18,g13)
    c: Coincident(g17,g13)
    c: Coincident(g5,g12)
    c: Coincident(g18,g12)
    c: Coincident(g6,g10)
    c: Coincident(g19,g10)
    c: PointOnObject(g19,g9)
    c: PointOnObject(g20,g9)
    c: PointOnObject(g20,g8)
    c: PointOnObject(g21,g8)
    c: PointOnObject(g21,g7)
    c: Coincident(g22,g7)
    c: Coincident(g22,g15)
    c: Coincident(g22,g7)
FEATURE [Sketcher::SketchObject] Sketch011
  FullyConstrained = false
  MapMode = 5
  Placement = pos=(0,0,0) rot=(0.57735,0.57735,0.57735;2.0944rad)
  Support = -> [YZ_Plane068]
  sketch-geometry (11):
    g0: Circle CenterX=0 CenterY=0 CenterZ=0 NormalX=0 NormalY=0 NormalZ=1 AngleXU=0 Radius=0.340608
    g1: Circle CenterX=1.26883 CenterY=0 CenterZ=0 NormalX=0 NormalY=0 NormalZ=1 AngleXU=0 Radius=0.340608
    g2: LineSegment StartX=0 StartY=0 StartZ=0 EndX=1.26883 EndY=0 EndZ=0
    g3: Circle CenterX=2.53767 CenterY=0 CenterZ=0 NormalX=0 NormalY=0 NormalZ=1 AngleXU=0 Radius=0.340608
    g4: LineSegment StartX=1.26883 StartY=0 StartZ=0 EndX=2.53767 EndY=0 EndZ=0
    g5: Circle CenterX=3.8065 CenterY=0 CenterZ=0 NormalX=0 NormalY=0 NormalZ=1 AngleXU=0 Radius=0.340608
    g6: LineSegment StartX=2.53767 StartY=0 StartZ=0 EndX=3.8065 EndY=0 EndZ=0
    g7: Circle CenterX=5.07533 CenterY=0 CenterZ=0 NormalX=0 NormalY=0 NormalZ=1 AngleXU=0 Radius=0.340608
    g8: LineSegment StartX=3.8065 StartY=0 StartZ=0 EndX=5.07533 EndY=0 EndZ=0
    g9: Circle CenterX=6.34417 CenterY=0 CenterZ=0 NormalX=0 NormalY=0 NormalZ=1 AngleXU=0 Radius=0.340608
    g10: LineSegment StartX=5.07533 StartY=0 StartZ=0 EndX=6.34417 EndY=0 EndZ=0
  constraints (21):
    c: Coincident(g0,g-1)
    c: Coincident(g0,g2)
    c: Coincident(g1,g2)
    c: Distance(g2) = 1.26883
    c: Angle(g2) = 0
    c: Coincident(g1,g4)
    c: Coincident(g3,g4)
    c: Equal(g2,g4)
    c: Parallel(g4,g2)
    c: Coincident(g3,g6)
    c: Coincident(g5,g6)
    c: Equal(g2,g6)
    c: Parallel(g6,g2)
    c: Coincident(g5,g8)
    c: Coincident(g7,g8)
    c: Equal(g2,g8)
    c: Parallel(g8,g2)
    c: Coincident(g7,g10)
    c: Coincident(g9,g10)
    c: Equal(g2,g10)
    c: Parallel(g10,g2)
FEATURE [Sketcher::SketchObject] Sketch012
  FullyConstrained = false
  MapMode = 5
  Placement = pos=(0,0,0) rot=(1,0,0;1.5708rad)
  sketch-geometry (7):
    g0-g3: Circle x4 (B-spline internal-alignment scaffolding for g4; pole/knot coordinates omitted)
    g4: BSplineCurve PolesCount=4 KnotsCount=2 Degree=3 IsPeriodic=0
    g5: GeomPoint X=0 Y=0 Z=0
    g6: GeomPoint X=-56.5564 Y=23 Z=0
  constraints (8):
    c: Weight(g0) = 1
    c: Coincident(g4,g-1)
    c: Equal(g0,g1)
    c: Equal(g0,g2)
    c: Equal(g0,g3)
    c: InternalAlignment(g0-g3 -> g4) x4
    c: InternalAlignment(g5,g4)
    c: InternalAlignment(g6,g4)
FEATURE [Sketcher::SketchObject] Sketch013
  FullyConstrained = false
  MapMode = 5
  Placement = pos=(0,0,0) rot=(0.57735,0.57735,0.57735;2.0944rad)
  sketch-geometry (26):
    g0: LineSegment StartX=0 StartY=0 StartZ=0 EndX=1.27335 EndY=0 EndZ=0
    g1: LineSegment StartX=0 StartY=0 StartZ=0 EndX=1.27103 EndY=0 EndZ=0
    g2: LineSegment StartX=1.27103 StartY=0 StartZ=0 EndX=2.54207 EndY=0 EndZ=0
    g3: LineSegment StartX=2.54207 StartY=0 StartZ=0 EndX=3.8131 EndY=0 EndZ=0
    g4: LineSegment StartX=3.8131 StartY=0 StartZ=0 EndX=5.08414 EndY=0 EndZ=0
    g5: ArcOfCircle CenterX=6.35517 CenterY=0 CenterZ=0 NormalX=0 NormalY=0 NormalZ=1 AngleXU=0 Radius=0.75 StartAngle=4.06889 EndAngle=8.49748
    g6: LineSegment StartX=5.08414 StartY=0 StartZ=0 EndX=6.35517 EndY=0 EndZ=0
    g7: LineSegment StartX=0.45 StartY=0.6 StartZ=0 EndX=0.821034 EndY=0.6 EndZ=0
    g8: LineSegment StartX=0.45 StartY=-0.6 StartZ=0 EndX=0.821034 EndY=-0.6 EndZ=0
    g9: ArcOfCircle CenterX=5.08414 CenterY=0 CenterZ=0 NormalX=0 NormalY=0 NormalZ=1 AngleXU=0 Radius=0.75 StartAngle=4.06889 EndAngle=5.35589
    g10: ArcOfCircle CenterX=3.8131 CenterY=0 CenterZ=0 NormalX=0 NormalY=0 NormalZ=1 AngleXU=0 Radius=0.75 StartAngle=4.06889 EndAngle=5.35589
    g11: ArcOfCircle CenterX=2.54207 CenterY=0 CenterZ=0 NormalX=0 NormalY=0 NormalZ=1 AngleXU=0 Radius=0.75 StartAngle=4.06889 EndAngle=5.35589
    g12: ArcOfCircle CenterX=1.27103 CenterY=0 CenterZ=0 NormalX=0 NormalY=0 NormalZ=1 AngleXU=0 Radius=0.75 StartAngle=4.06889 EndAngle=5.35589
    g13: ArcOfCircle CenterX=0 CenterY=0 CenterZ=0 NormalX=0 NormalY=0 NormalZ=1 AngleXU=0 Radius=0.75 StartAngle=0.927295 EndAngle=5.35589
    g14: ArcOfCircle CenterX=1.27103 CenterY=0 CenterZ=0 NormalX=0 NormalY=0 NormalZ=1 AngleXU=0 Radius=0.75 StartAngle=0.927295 EndAngle=2.2143
    g15: ArcOfCircle CenterX=2.54207 CenterY=0 CenterZ=0 NormalX=0 NormalY=0 NormalZ=1 AngleXU=0 Radius=0.75 StartAngle=0.927295 EndAngle=2.2143
    g16: ArcOfCircle CenterX=3.8131 CenterY=0 CenterZ=0 NormalX=0 NormalY=0 NormalZ=1 AngleXU=0 Radius=0.75 StartAngle=0.927295 EndAngle=2.2143
    g17: ArcOfCircle CenterX=5.08414 CenterY=0 CenterZ=0 NormalX=0 NormalY=0 NormalZ=1 AngleXU=0 Radius=0.75 StartAngle=0.927295 EndAngle=2.2143
    g18: LineSegment StartX=5.53414 StartY=0.6 StartZ=0 EndX=5.90517 EndY=0.6 EndZ=0
    g19: LineSegment StartX=4.2631 StartY=0.6 StartZ=0 EndX=4.63414 EndY=0.6 EndZ=0
    g20: LineSegment StartX=2.99207 StartY=0.6 StartZ=0 EndX=3.3631 EndY=0.6 EndZ=0
    g21: LineSegment StartX=1.72103 StartY=0.6 StartZ=0 EndX=2.09207 EndY=0.6 EndZ=0
    g22: LineSegment StartX=1.72103 StartY=-0.6 StartZ=0 EndX=2.09207 EndY=-0.6 EndZ=0
    g23: LineSegment StartX=2.99207 StartY=-0.6 StartZ=0 EndX=3.3631 EndY=-0.6 EndZ=0
    g24: LineSegment StartX=4.2631 StartY=-0.6 StartZ=0 EndX=4.63414 EndY=-0.6 EndZ=0
    g25: LineSegment StartX=5.53414 StartY=-0.6 StartZ=0 EndX=5.90517 EndY=-0.6 EndZ=0
  constraints (41):
    c: Angle(g0) = 0
    c: Distance(g1) = 1.27103
    c: Angle(g1) = 0
    c: Equal(g1,g2)
    c: Parallel(g2,g1)
    c: Equal(g1,g3)
    c: Parallel(g3,g1)
    c: Equal(g1,g4)
    c: Parallel(g4,g1)
    c: Radius(g5) = 0.75
    c: Coincident(g5,g6)
    c: Equal(g1,g6)
    c: Parallel(g6,g1)
    c: Horizontal(g7)
    c: Horizontal(g8)
    c: Coincident(g5,g25)
    c: PointOnObject(g9,g8)
    c: PointOnObject(g9,g8)
    c: PointOnObject(g10,g8)
    c: PointOnObject(g10,g8)
    c: PointOnObject(g11,g8)
    c: PointOnObject(g11,g8)
    c: Coincident(g8,g13)
    c: Coincident(g13,g7)
    c: Coincident(g18,g5)
    c: Coincident(g19,g17)
    c: Coincident(g18,g17)
    c: Coincident(g20,g16)
    c: Coincident(g19,g16)
    c: Coincident(g21,g15)
    c: Coincident(g20,g15)
    c: Coincident(g7,g14)
    c: Coincident(g21,g14)
    c: Coincident(g8,g12)
    c: Coincident(g22,g12)
    c: PointOnObject(g22,g11)
    c: PointOnObject(g23,g11)
    c: PointOnObject(g23,g10)
    c: PointOnObject(g24,g10)
    c: PointOnObject(g24,g9)
    c: PointOnObject(g25,g9)
FEATURE [PartDesign::Pad] Pad003
  Direction = (1,0,0)
  Length = 1
  Length2 = 10
  Placement = pos=(0,0,0) rot=(0.57735,0.57735,0.57735;2.0944rad)
  Profile = -> Sketch013
  ReferenceAxis = -> Sketch013 [N_Axis]
  Type = 0
FEATURE [PartDesign::Pad] Pad004
  BaseFeature = -> Pad003
  Direction = (1,-2e-16,3e-16)
  Length = 6
  Length2 = 10
  Placement = pos=(0,0,0) rot=(0.57735,0.57735,0.57735;2.0944rad)
  Profile = -> Sketch011
  ReferenceAxis = -> Sketch011 [N_Axis]
  Type = 0
FEATURE [PartDesign::Body] Body003
  Group = -> [Sketch011,Sketch013,Pad003,Pad004]
  Origin = -> Origin068
  Placement = pos=(44.25,0,12.5) rot=(0,0,1;0rad)
  Tip = -> Pad004
FEATURE [Sketcher::SketchObject] Sketch014
  FullyConstrained = false
  MapMode = 5
  Placement = pos=(0,0,0) rot=(0.57735,0.57735,0.57735;2.0944rad)
  sketch-geometry (2):
    g0: ArcOfCircle CenterX=6.35517 CenterY=-2.69756e-08 CenterZ=0 NormalX=0 NormalY=0 NormalZ=1 AngleXU=0 Radius=0.75 StartAngle=4.06889 EndAngle=8.49748
    g1: ArcOfCircle CenterX=6.35517 CenterY=-2.69756e-08 CenterZ=0 NormalX=0 NormalY=0 NormalZ=1 AngleXU=0 Radius=0.75 StartAngle=2.2143 EndAngle=4.06889
  constraints (4):
    c: Radius(g0) = 0.75
    c: Coincident(g1,g0)
    c: Coincident(g1,g0)
    c: Coincident(g1,g0)
FEATURE [Sketcher::SketchObject] Sketch015
  FullyConstrained = false
  MapMode = 5
  Placement = pos=(0,0,0) rot=(1,0,0;1.5708rad)
  sketch-geometry (7):
    g0-g3: Circle x4 (B-spline internal-alignment scaffolding for g4; pole/knot coordinates omitted)
    g4: BSplineCurve PolesCount=4 KnotsCount=2 Degree=3 IsPeriodic=0
    g5: GeomPoint X=0 Y=2.18e-14 Z=0
    g6: GeomPoint X=-56.5753 Y=23.0036 Z=0
  constraints (8):
    c: Weight(g0) = 1
    c: Coincident(g4,g-1)
    c: Equal(g0,g1)
    c: Equal(g0,g2)
    c: Equal(g0,g3)
    c: InternalAlignment(g0-g3 -> g4) x4
    c: InternalAlignment(g5,g4)
    c: InternalAlignment(g6,g4)
FEATURE [Part::Sweep] Sweep002
  Frenet = false
  Placement = pos=(45,0,12.5) rot=(0,0,1;0rad)
  Sections = -> [Sketch010]
  Solid = false
  Spine = -> Sketch012 [Edge1]
  Transition = 1
FEATURE [Part::Sweep] Sweep003
  Frenet = false
  Placement = pos=(45,0,12.5) rot=(0,0,1;0rad)
  Sections = -> [Sketch014]
  Solid = false
  Spine = -> Sketch015 [Edge1]
  Transition = 1
FEATURE [App::Part] Part007  label="idc-cable_before_pipe"
  Group = -> [Body003,Sketch012,Sketch010,Sweep002,Sketch014,Sketch015,Sweep003]
  Origin = -> Origin069
  Placement = pos=(-3,-1.25,50.25) rot=(-0.57735,-0.57735,0.57735;4.18879rad)
FEATURE [App::VRMLObject] _90157000672002  label="690157000672001001"
FEATURE [App::Part] Part008  label="idc-plug_before_pipe"
  Group = -> [_90157000672002]
  Origin = -> Origin070
  Placement = pos=(-2.43e-14,-36.9321,59.2771) rot=(-1,0,0;1.5708rad)
FEATURE [Part::Feature] Part__Feature104  label="SOLID044"
  shape: bbox 5.2 x 5.3 x 3 mm, 19 faces (baked)
FEATURE [Part::Feature] Part__Feature105  label="SOLID045"
  shape: bbox 0.25 x 5.15 x 5.25 mm, 43 faces (baked)
FEATURE [Part::Feature] Part__Feature106  label="SOLID046"
  shape: bbox 0.25 x 5.15 x 5.25 mm, 43 faces (baked)
FEATURE [Part::Feature] Part__Feature107  label="SOLID047"
  shape: bbox 0.25 x 5.15 x 5.25 mm, 43 faces (baked)
FEATURE [Part::Feature] Part__Feature108  label="SOLID048"
  shape: bbox 0.25 x 5.15 x 5.25 mm, 43 faces (baked)
FEATURE [Part::Feature] Part__Feature109  label="SOLID049"
  shape: bbox 0.25 x 5.15 x 5.25 mm, 43 faces (baked)
FEATURE [Part::Feature] Part__Feature110  label="SOLID050"
  shape: bbox 0.25 x 5.15 x 5.25 mm, 43 faces (baked)
FEATURE [Part::Feature] Part__Feature111  label="SOLID051"
  shape: bbox 9.62 x 5 x 5 mm, 276 faces (baked)
FEATURE [App::Part] _90367280676_1  label="690367280676_step"
  Group = -> [Part__Feature104,Part__Feature105,Part__Feature106,Part__Feature107,Part__Feature108,Part__Feature109,Part__Feature110,Part__Feature111]
  Origin = -> Origin071
  Placement = pos=(76.25,-84,4.25) rot=(0,0,1;0rad)
FEATURE [App::Part] Part  label="smd"
  Group = -> [ArduinoNanoRP2040,Honeywell_MPRL,PinSocket_1x04_P2_54mm_Vertical_SMD_Pin1Right,C_1210_3225Metric,C_0603_1608Metric003,SOT_23,Buzzer_Murata_PKMCS0909E4000_R1,SFH4045N003,_90367280676,SFH4045N002,R_0603_1608Metric002,C_0603_1608Metric,SFH4045N,D_SOD_323,R_0603_1608Metric,C_0603_1608Metric001,D_SOD_323001,R_0603_1608Metric001,C_0603_1608Metric002,SFH4045N001,_90367280676_1]
  Origin = -> Origin029
FEATURE [App::Part] FM3_mainboard_1  label="FM3_mainboard 1"
  Group = -> [FC68125,LED_D5_0mm_Horizontal_O3_81mm_Z9_0mm,LED_D5_0mm_Horizontal_O3_81mm_Z9_0mm001,SW_Tactile_SPST_Angled_PTS645Vx58_2LFS,FC68125001,Vishay_MOLD_3Pin,Part__Feature028,Part]
  Origin = -> Origin028
FEATURE [App::Part] Part001  label="mainboard"
  Group = -> [FM3_mainboard_1,ImagePlane,ImagePlane001]
  Origin = -> Origin035
  Placement = pos=(30.75,76,-8.5) rot=(0,0,1;4.71239rad)
FEATURE [PartDesign::AdditivePipe] AdditivePipe
  AuxilleryCurvelinear = true
  AuxillerySpineTangent = false
  Binormal = (0,0,0)
  Mode = 0
  Placement = pos=(0,0,0) rot=(0.57735,0.57735,0.57735;2.0944rad)
  Profile = -> Sketch008
  Spine = -> Sketch009 [Edge1]
  SpineTangent = false
  Transformation = 0
  Transition = 0
FEATURE [PartDesign::Body] Body002  label="2x4_long_mounted"
  Group = -> [Sketch008,Sketch009,AdditivePipe]
  Origin = -> Origin067
  Tip = -> AdditivePipe
FEATURE [Image::ImagePlane] ImagePlane004  label="mouthpiece"
  Placement = pos=(60.75,-7.4e-15,0) rot=(0,0.130526,-0.991445;3.14159rad)
  XSize = 100
  YSize = 10
FEATURE [Sketcher::SketchObject] Sketch016  label="diameter001"
  FullyConstrained = true
  MapMode = 5
  Placement = pos=(0,0,0) rot=(0.57735,0.57735,0.57735;2.0944rad)
  Support = -> [YZ_Plane072]
  sketch-geometry (2):
    g0: Circle CenterX=0 CenterY=0 CenterZ=0 NormalX=0 NormalY=0 NormalZ=1 AngleXU=0 Radius=1
    g1: Circle CenterX=0 CenterY=0 CenterZ=0 NormalX=0 NormalY=0 NormalZ=1 AngleXU=0 Radius=2
  constraints (4):
    c: Coincident(g0,g-1)
    c: Radius(g0) = 1
    c: Coincident(g1,g0)
    c: Radius(g1) = 2
FEATURE [Sketcher::SketchObject] Sketch017  label="sweep001"
  FullyConstrained = false
  MapMode = 5
  Placement = pos=(0,0,0) rot=(1,0,0;1.5708rad)
  Support = -> [XZ_Plane072]
  sketch-geometry (7):
    g0-g3: Circle x4 (B-spline internal-alignment scaffolding for g4; pole/knot coordinates omitted)
    g4: BSplineCurve PolesCount=4 KnotsCount=2 Degree=3 IsPeriodic=0
    g5: GeomPoint X=0.136781 Y=0.055561 Z=0
    g6: GeomPoint X=-47.8364 Y=-0.041645 Z=0
  constraints (7):
    c: Weight(g0) = 1
    c: Equal(g0,g1)
    c: Equal(g0,g2)
    c: Equal(g0,g3)
    c: InternalAlignment(g0-g3 -> g4) x4
    c: InternalAlignment(g5,g4)
    c: InternalAlignment(g6,g4)
FEATURE [PartDesign::AdditivePipe] AdditivePipe001
  AuxilleryCurvelinear = true
  AuxillerySpineTangent = false
  Binormal = (0,0,0)
  Mode = 0
  Placement = pos=(0,0,0) rot=(0.57735,0.57735,0.57735;2.0944rad)
  Profile = -> Sketch016
  Spine = -> Sketch017 [Edge1]
  SpineTangent = false
  Transformation = 0
  Transition = 0
FEATURE [PartDesign::Body] Body004  label="2x4_long_straight"
  Group = -> [Sketch016,Sketch017,AdditivePipe001]
  Origin = -> Origin072
  Tip = -> AdditivePipe001
FEATURE [App::Part] Part006  label="tubes"
  Group = -> [Body,Body002,Body004]
  Origin = -> Origin065
  Placement = pos=(-40,0,1.25) rot=(0,1,0;1.5708rad)
FEATURE [App::VRMLObject] RES_DMS_NAU7802  label="RES-DMS-NAU7802"
  Resources = RES_DMS_NAU7802/R_1206_3216Metric.wrl | RES_DMS_NAU7802/ | RES_DMS_NAU7802/ | RES_DMS_NAU7802/ | RES_DMS_NAU7802/ | RES_DMS_NAU7802/
FEATURE [App::Part] Part009  label="PCB"
  Group = -> [RES_DMS_NAU7802]
  Origin = -> Origin073
  Placement = pos=(10,-2.4e-15,2) rot=(0,0,1;3.14159rad)
FEATURE [Part::Feature] Part__Feature112  label="female luer lock 37"
FEATURE [App::Part] Part010  label="luer"
  Group = -> [Part__Feature112]
  Origin = -> Origin074
  Placement = pos=(0,-1.3e-15,-6) rot=(1,0,0;1.5708rad)
FEATURE [Mesh::Feature] FM3_case_front_white  label="FM3_case-front_white"
  Placement = pos=(2,0,0) rot=(0,0,1;0rad)
FEATURE [Mesh::Feature] FM3_case_base  label="FM3_case-base"
FEATURE [Sketcher::SketchObject] Sketch018
  FullyConstrained = false
  MapMode = 5
  Placement = pos=(0,0,0) rot=(0.57735,0.57735,0.57735;2.0944rad)
  sketch-geometry (23):
    g0: LineSegment StartX=0 StartY=0 StartZ=0 EndX=1.27335 EndY=0 EndZ=0
    g1: LineSegment StartX=0 StartY=0 StartZ=0 EndX=1.27103 EndY=0 EndZ=0
    g2: LineSegment StartX=1.27103 StartY=0 StartZ=0 EndX=2.54207 EndY=0 EndZ=0
    g3: LineSegment StartX=2.54207 StartY=0 StartZ=0 EndX=3.8131 EndY=0 EndZ=0
    g4: LineSegment StartX=3.8131 StartY=0 StartZ=0 EndX=5.08414 EndY=0 EndZ=0
    g5: LineSegment StartX=0.45 StartY=0.6 StartZ=0 EndX=0.821034 EndY=0.6 EndZ=0
    g6: LineSegment StartX=0.45 StartY=-0.6 StartZ=0 EndX=0.821034 EndY=-0.6 EndZ=0
    g7: ArcOfCircle CenterX=5.08414 CenterY=7.1e-15 CenterZ=0 NormalX=0 NormalY=0 NormalZ=1 AngleXU=0 Radius=0.75 StartAngle=4.06889 EndAngle=5.35589
    g8: ArcOfCircle CenterX=3.8131 CenterY=0 CenterZ=0 NormalX=0 NormalY=0 NormalZ=1 AngleXU=0 Radius=0.75 StartAngle=4.06889 EndAngle=5.35589
    g9: ArcOfCircle CenterX=2.54207 CenterY=0 CenterZ=0 NormalX=0 NormalY=0 NormalZ=1 AngleXU=0 Radius=0.75 StartAngle=4.06889 EndAngle=5.35589
    g10: ArcOfCircle CenterX=1.27103 CenterY=-2e-16 CenterZ=0 NormalX=0 NormalY=0 NormalZ=1 AngleXU=0 Radius=0.75 StartAngle=4.06889 EndAngle=5.35589
    g11: ArcOfCircle CenterX=0 CenterY=-1e-16 CenterZ=0 NormalX=0 NormalY=0 NormalZ=1 AngleXU=0 Radius=0.75 StartAngle=0.927295 EndAngle=5.35589
    g12: ArcOfCircle CenterX=1.27103 CenterY=0 CenterZ=0 NormalX=0 NormalY=0 NormalZ=1 AngleXU=0 Radius=0.75 StartAngle=0.927295 EndAngle=2.2143
    g13: ArcOfCircle CenterX=2.54207 CenterY=0 CenterZ=0 NormalX=0 NormalY=0 NormalZ=1 AngleXU=0 Radius=0.75 StartAngle=0.927295 EndAngle=2.2143
    g14: ArcOfCircle CenterX=3.8131 CenterY=0 CenterZ=0 NormalX=0 NormalY=0 NormalZ=1 AngleXU=0 Radius=0.75 StartAngle=0.927295 EndAngle=2.2143
    g15: ArcOfCircle CenterX=5.08414 CenterY=-9.81007e-08 CenterZ=0 NormalX=0 NormalY=0 NormalZ=1 AngleXU=0 Radius=0.75 StartAngle=0.927295 EndAngle=2.2143
    g16: LineSegment StartX=4.2631 StartY=0.6 StartZ=0 EndX=4.63414 EndY=0.6 EndZ=0
    g17: LineSegment StartX=2.99207 StartY=0.6 StartZ=0 EndX=3.3631 EndY=0.6 EndZ=0
    g18: LineSegment StartX=1.72103 StartY=0.6 StartZ=0 EndX=2.09207 EndY=0.6 EndZ=0
    g19: LineSegment StartX=1.72103 StartY=-0.6 StartZ=0 EndX=2.09207 EndY=-0.6 EndZ=0
    g20: LineSegment StartX=2.99207 StartY=-0.6 StartZ=0 EndX=3.3631 EndY=-0.6 EndZ=0
    g21: LineSegment StartX=4.2631 StartY=-0.6 StartZ=0 EndX=4.63414 EndY=-0.6 EndZ=0
    g22: ArcOfCircle CenterX=5.08414 CenterY=7.1e-15 CenterZ=0 NormalX=0 NormalY=0 NormalZ=1 AngleXU=0 Radius=0.75 StartAngle=5.35589 EndAngle=7.21048
  constraints (36):
    c: Angle(g0) = 0
    c: Distance(g1) = 1.27103
    c: Angle(g1) = 0
    c: Equal(g1,g2)
    c: Parallel(g2,g1)
    c: Equal(g1,g3)
    c: Parallel(g3,g1)
    c: Equal(g1,g4)
    c: Parallel(g4,g1)
    c: Horizontal(g5)
    c: Horizontal(g6)
    c: PointOnObject(g7,g6)
    c: PointOnObject(g7,g6)
    c: PointOnObject(g8,g6)
    c: PointOnObject(g8,g6)
    c: PointOnObject(g9,g6)
    c: PointOnObject(g9,g6)
    c: Coincident(g6,g11)
    c: Coincident(g11,g5)
    c: Coincident(g16,g15)
    c: Coincident(g17,g14)
    c: Coincident(g16,g14)
    c: Coincident(g18,g13)
    c: Coincident(g17,g13)
    c: Coincident(g5,g12)
    c: Coincident(g18,g12)
    c: Coincident(g6,g10)
    c: Coincident(g19,g10)
    c: PointOnObject(g19,g9)
    c: PointOnObject(g20,g9)
    c: PointOnObject(g20,g8)
    c: PointOnObject(g21,g8)
    c: PointOnObject(g21,g7)
    c: Coincident(g22,g7)
    c: Coincident(g22,g15)
    c: Coincident(g22,g7)
FEATURE [Sketcher::SketchObject] Sketch019
  FullyConstrained = false
  MapMode = 5
  Placement = pos=(0,0,0) rot=(0.57735,0.57735,0.57735;2.0944rad)
  Support = -> [YZ_Plane075]
  sketch-geometry (11):
    g0: Circle CenterX=0 CenterY=0 CenterZ=0 NormalX=0 NormalY=0 NormalZ=1 AngleXU=0 Radius=0.340608
    g1: Circle CenterX=1.26883 CenterY=0 CenterZ=0 NormalX=0 NormalY=0 NormalZ=1 AngleXU=0 Radius=0.340608
    g2: LineSegment StartX=0 StartY=0 StartZ=0 EndX=1.26883 EndY=0 EndZ=0
    g3: Circle CenterX=2.53767 CenterY=0 CenterZ=0 NormalX=0 NormalY=0 NormalZ=1 AngleXU=0 Radius=0.340608
    g4: LineSegment StartX=1.26883 StartY=0 StartZ=0 EndX=2.53767 EndY=0 EndZ=0
    g5: Circle CenterX=3.8065 CenterY=0 CenterZ=0 NormalX=0 NormalY=0 NormalZ=1 AngleXU=0 Radius=0.340608
    g6: LineSegment StartX=2.53767 StartY=0 StartZ=0 EndX=3.8065 EndY=0 EndZ=0
    g7: Circle CenterX=5.07533 CenterY=0 CenterZ=0 NormalX=0 NormalY=0 NormalZ=1 AngleXU=0 Radius=0.340608
    g8: LineSegment StartX=3.8065 StartY=0 StartZ=0 EndX=5.07533 EndY=0 EndZ=0
    g9: Circle CenterX=6.34417 CenterY=0 CenterZ=0 NormalX=0 NormalY=0 NormalZ=1 AngleXU=0 Radius=0.340608
    g10: LineSegment StartX=5.07533 StartY=0 StartZ=0 EndX=6.34417 EndY=0 EndZ=0
  constraints (21):
    c: Coincident(g0,g-1)
    c: Coincident(g0,g2)
    c: Coincident(g1,g2)
    c: Distance(g2) = 1.26883
    c: Angle(g2) = 0
    c: Coincident(g1,g4)
    c: Coincident(g3,g4)
    c: Equal(g2,g4)
    c: Parallel(g4,g2)
    c: Coincident(g3,g6)
    c: Coincident(g5,g6)
    c: Equal(g2,g6)
    c: Parallel(g6,g2)
    c: Coincident(g5,g8)
    c: Coincident(g7,g8)
    c: Equal(g2,g8)
    c: Parallel(g8,g2)
    c: Coincident(g7,g10)
    c: Coincident(g9,g10)
    c: Equal(g2,g10)
    c: Parallel(g10,g2)
FEATURE [Sketcher::SketchObject] Sketch020
  FullyConstrained = false
  MapMode = 5
  Placement = pos=(0,0,0) rot=(1,0,0;1.5708rad)
  sketch-geometry (11):
    g0-g5: Circle x6 (B-spline internal-alignment scaffolding for g6; pole/knot coordinates omitted)
    g6: BSplineCurve PolesCount=6 KnotsCount=4 Degree=3 IsPeriodic=0
    g7-g10: GeomPoint x4 (B-spline internal-alignment scaffolding for g6; pole/knot coordinates omitted)
  constraints (4):
    c: Weight(g0) = 1
    c: Equal(g0, g1-g5) x5
    c: InternalAlignment(g0-g5 -> g6) x6
    c: InternalAlignment(g7-g10 -> g6) x4
FEATURE [Sketcher::SketchObject] Sketch021
  FullyConstrained = false
  MapMode = 5
  Placement = pos=(0,0,0) rot=(0.57735,0.57735,0.57735;2.0944rad)
  sketch-geometry (26):
    g0: LineSegment StartX=0 StartY=0 StartZ=0 EndX=1.27335 EndY=0 EndZ=0
    g1: LineSegment StartX=0 StartY=0 StartZ=0 EndX=1.27103 EndY=0 EndZ=0
    g2: LineSegment StartX=1.27103 StartY=0 StartZ=0 EndX=2.54207 EndY=0 EndZ=0
    g3: LineSegment StartX=2.54207 StartY=0 StartZ=0 EndX=3.8131 EndY=0 EndZ=0
    g4: LineSegment StartX=3.8131 StartY=0 StartZ=0 EndX=5.08414 EndY=0 EndZ=0
    g5: ArcOfCircle CenterX=6.35517 CenterY=0 CenterZ=0 NormalX=0 NormalY=0 NormalZ=1 AngleXU=0 Radius=0.75 StartAngle=4.06889 EndAngle=8.49748
    g6: LineSegment StartX=5.08414 StartY=0 StartZ=0 EndX=6.35517 EndY=0 EndZ=0
    g7: LineSegment StartX=0.45 StartY=0.6 StartZ=0 EndX=0.821034 EndY=0.6 EndZ=0
    g8: LineSegment StartX=0.45 StartY=-0.6 StartZ=0 EndX=0.821034 EndY=-0.6 EndZ=0
    g9: ArcOfCircle CenterX=5.08414 CenterY=0 CenterZ=0 NormalX=0 NormalY=0 NormalZ=1 AngleXU=0 Radius=0.75 StartAngle=4.06889 EndAngle=5.35589
    g10: ArcOfCircle CenterX=3.8131 CenterY=0 CenterZ=0 NormalX=0 NormalY=0 NormalZ=1 AngleXU=0 Radius=0.75 StartAngle=4.06889 EndAngle=5.35589
    g11: ArcOfCircle CenterX=2.54207 CenterY=0 CenterZ=0 NormalX=0 NormalY=0 NormalZ=1 AngleXU=0 Radius=0.75 StartAngle=4.06889 EndAngle=5.35589
    g12: ArcOfCircle CenterX=1.27103 CenterY=0 CenterZ=0 NormalX=0 NormalY=0 NormalZ=1 AngleXU=0 Radius=0.75 StartAngle=4.06889 EndAngle=5.35589
    g13: ArcOfCircle CenterX=0 CenterY=0 CenterZ=0 NormalX=0 NormalY=0 NormalZ=1 AngleXU=0 Radius=0.75 StartAngle=0.927295 EndAngle=5.35589
    g14: ArcOfCircle CenterX=1.27103 CenterY=0 CenterZ=0 NormalX=0 NormalY=0 NormalZ=1 AngleXU=0 Radius=0.75 StartAngle=0.927295 EndAngle=2.2143
    g15: ArcOfCircle CenterX=2.54207 CenterY=0 CenterZ=0 NormalX=0 NormalY=0 NormalZ=1 AngleXU=0 Radius=0.75 StartAngle=0.927295 EndAngle=2.2143
    g16: ArcOfCircle CenterX=3.8131 CenterY=0 CenterZ=0 NormalX=0 NormalY=0 NormalZ=1 AngleXU=0 Radius=0.75 StartAngle=0.927295 EndAngle=2.2143
    g17: ArcOfCircle CenterX=5.08414 CenterY=0 CenterZ=0 NormalX=0 NormalY=0 NormalZ=1 AngleXU=0 Radius=0.75 StartAngle=0.927295 EndAngle=2.2143
    g18: LineSegment StartX=5.53414 StartY=0.6 StartZ=0 EndX=5.90517 EndY=0.6 EndZ=0
    g19: LineSegment StartX=4.2631 StartY=0.6 StartZ=0 EndX=4.63414 EndY=0.6 EndZ=0
    g20: LineSegment StartX=2.99207 StartY=0.6 StartZ=0 EndX=3.3631 EndY=0.6 EndZ=0
    g21: LineSegment StartX=1.72103 StartY=0.6 StartZ=0 EndX=2.09207 EndY=0.6 EndZ=0
    g22: LineSegment StartX=1.72103 StartY=-0.6 StartZ=0 EndX=2.09207 EndY=-0.6 EndZ=0
    g23: LineSegment StartX=2.99207 StartY=-0.6 StartZ=0 EndX=3.3631 EndY=-0.6 EndZ=0
    g24: LineSegment StartX=4.2631 StartY=-0.6 StartZ=0 EndX=4.63414 EndY=-0.6 EndZ=0
    g25: LineSegment StartX=5.53414 StartY=-0.6 StartZ=0 EndX=5.90517 EndY=-0.6 EndZ=0
  constraints (41):
    c: Angle(g0) = 0
    c: Distance(g1) = 1.27103
    c: Angle(g1) = 0
    c: Equal(g1,g2)
    c: Parallel(g2,g1)
    c: Equal(g1,g3)
    c: Parallel(g3,g1)
    c: Equal(g1,g4)
    c: Parallel(g4,g1)
    c: Radius(g5) = 0.75
    c: Coincident(g5,g6)
    c: Equal(g1,g6)
    c: Parallel(g6,g1)
    c: Horizontal(g7)
    c: Horizontal(g8)
    c: Coincident(g5,g25)
    c: PointOnObject(g9,g8)
    c: PointOnObject(g9,g8)
    c: PointOnObject(g10,g8)
    c: PointOnObject(g10,g8)
    c: PointOnObject(g11,g8)
    c: PointOnObject(g11,g8)
    c: Coincident(g8,g13)
    c: Coincident(g13,g7)
    c: Coincident(g18,g5)
    c: Coincident(g19,g17)
    c: Coincident(g18,g17)
    c: Coincident(g20,g16)
    c: Coincident(g19,g16)
    c: Coincident(g21,g15)
    c: Coincident(g20,g15)
    c: Coincident(g7,g14)
    c: Coincident(g21,g14)
    c: Coincident(g8,g12)
    c: Coincident(g22,g12)
    c: PointOnObject(g22,g11)
    c: PointOnObject(g23,g11)
    c: PointOnObject(g23,g10)
    c: PointOnObject(g24,g10)
    c: PointOnObject(g24,g9)
    c: PointOnObject(g25,g9)
FEATURE [PartDesign::Pad] Pad005
  Direction = (1,0,0)
  Length = 1
  Length2 = 10
  Placement = pos=(0,0,0) rot=(0.57735,0.57735,0.57735;2.0944rad)
  Profile = -> Sketch021
  ReferenceAxis = -> Sketch021 [N_Axis]
  Type = 0
FEATURE [PartDesign::Pad] Pad006
  BaseFeature = -> Pad005
  Direction = (1,-2e-16,3e-16)
  Length = 6
  Length2 = 10
  Placement = pos=(0,0,0) rot=(0.57735,0.57735,0.57735;2.0944rad)
  Profile = -> Sketch019
  ReferenceAxis = -> Sketch019 [N_Axis]
  Type = 0
FEATURE [PartDesign::Body] Body005
  Group = -> [Sketch019,Sketch021,Pad005,Pad006]
  Origin = -> Origin075
  Placement = pos=(44.25,0,12.5) rot=(0,0,1;0rad)
  Tip = -> Pad006
FEATURE [Sketcher::SketchObject] Sketch022
  FullyConstrained = false
  MapMode = 5
  Placement = pos=(0,0,0) rot=(0.57735,0.57735,0.57735;2.0944rad)
  sketch-geometry (2):
    g0: ArcOfCircle CenterX=6.35517 CenterY=-2.69756e-08 CenterZ=0 NormalX=0 NormalY=0 NormalZ=1 AngleXU=0 Radius=0.75 StartAngle=4.06889 EndAngle=8.49748
    g1: ArcOfCircle CenterX=6.35517 CenterY=-2.69756e-08 CenterZ=0 NormalX=0 NormalY=0 NormalZ=1 AngleXU=0 Radius=0.75 StartAngle=2.2143 EndAngle=4.06889
  constraints (4):
    c: Radius(g0) = 0.75
    c: Coincident(g1,g0)
    c: Coincident(g1,g0)
    c: Coincident(g1,g0)
FEATURE [Sketcher::SketchObject] Sketch023
  FullyConstrained = false
  MapMode = 5
  Placement = pos=(0,0,0) rot=(1,0,0;1.5708rad)
  sketch-geometry (11):
    g0-g5: Circle x6 (B-spline internal-alignment scaffolding for g6; pole/knot coordinates omitted)
    g6: BSplineCurve PolesCount=6 KnotsCount=4 Degree=3 IsPeriodic=0
    g7-g10: GeomPoint x4 (B-spline internal-alignment scaffolding for g6; pole/knot coordinates omitted)
  constraints (4):
    c: Weight(g0) = 1
    c: Equal(g0, g1-g5) x5
    c: InternalAlignment(g0-g5 -> g6) x6
    c: InternalAlignment(g7-g10 -> g6) x4
FEATURE [Part::Sweep] Sweep004
  Frenet = false
  Sections = -> [Sketch018]
  Solid = false
  Spine = -> Sketch020 [Edge1]
  Transition = 1
FEATURE [Part::Sweep] Sweep005
  Frenet = false
  Sections = -> [Sketch022]
  Solid = false
  Spine = -> Sketch023 [Edge1]
  Transition = 1
FEATURE [App::Part] Part011  label="idc-cable_sensor"
  Group = -> [Body005,Sketch020,Sketch018,Sweep004,Sketch022,Sketch023,Sweep005]
  Origin = -> Origin076
  Placement = pos=(17.1885,-12.5637,18.2408) rot=(-0.91712,0.379884,0.120741;3.24153rad)
FEATURE [App::VRMLObject] _90157000672003  label="690157000672001002"
FEATURE [App::Part] Part012  label="idc-plug_sensor"
  Group = -> [_90157000672003]
  Origin = -> Origin077
  Placement = pos=(10.0919,-8.88682,20.2248) rot=(0.366573,-0.929137,0.04826;3.0968rad)
FEATURE [App::Part] Part005  label="sensorboard+cable"
  Group = -> [Part003,Part004,Part007,Part008,Part009,Part010,Part011,Part012]
  Origin = -> Origin064
  Placement = pos=(-0.25,1e-16,-1e-16) rot=(0.57735,0.57735,-0.57735;4.18879rad)
FEATURE [App::VRMLObject] sensorboard_MPRLS  label="sensorboard_DPS310"
FEATURE [Part::Feature] Part__Feature113  label="SOLID052"
FEATURE [App::Part] C_0603_1608Metric004
  Group = -> [Part__Feature113]
  Origin = -> Origin078
  Placement = pos=(70.4,-42.375,1.63) rot=(0,0,1;3.14159rad)
FEATURE [Part::Feature] Part__Feature114  label="SOLID053"
FEATURE [App::Part] SFH4045N004
  Group = -> [Part__Feature114]
  Origin = -> Origin079
  Placement = pos=(66.4,-99.3,2.22) rot=(0.57735,-0.57735,0.57735;2.0944rad)
FEATURE [Part::Feature] Part__Feature115  label="SOLID054"
FEATURE [App::Part] D_SOD_323002  label="D_SOD-325"
  Group = -> [Part__Feature115]
  Origin = -> Origin080
  Placement = pos=(74,-42.4,1.63) rot=(0,0,1;0rad)
FEATURE [Part::Feature] Part__Feature116  label="SOLID055"
FEATURE [App::Part] R_0603_1608Metric003
  Group = -> [Part__Feature116]
  Origin = -> Origin081
  Placement = pos=(86,-92.9,1.63) rot=(0,0,1;0rad)
FEATURE [Part::Feature] Part__Feature117  label="COMPOUND"
FEATURE [App::Part] FC68125002
  Group = -> [Part__Feature117]
  Origin = -> Origin082
  Placement = pos=(62.1,-49.75,1.63) rot=(0,0,-1;1.5708rad)
FEATURE [Part::Feature] Part__Feature118  label="SOLID056"
FEATURE [App::Part] C_0603_1608Metric005
  Group = -> [Part__Feature118]
  Origin = -> Origin083
  Placement = pos=(81.6,-42.4,1.63) rot=(0,0,1;0rad)
FEATURE [Part::Feature] Part__Feature119  label="SOLID057"
FEATURE [App::Part] C_0603_1608Metric006
  Group = -> [Part__Feature119]
  Origin = -> Origin084
  Placement = pos=(71.1,-77.6,1.63) rot=(0,0,-1;1.5708rad)
FEATURE [Part::Feature] Part__Feature120  label="SOLID058"
FEATURE [App::Part] D_SOD_323003  label="D_SOD-326"
  Group = -> [Part__Feature120]
  Origin = -> Origin085
  Placement = pos=(78,-42.4,1.63) rot=(0,0,1;3.14159rad)
FEATURE [Part::Feature] Part__Feature121  label="SOLID059"
FEATURE [App::Part] R_0603_1608Metric004
  Group = -> [Part__Feature121]
  Origin = -> Origin086
  Placement = pos=(82.7,-93.9,1.63) rot=(0,0,1;1.5708rad)
FEATURE [Part::Feature] Part__Feature122  label="SOLID060"
FEATURE [App::Part] SW_Tactile_SPST_Angled_PTS645Vx58_2LFS001  label="SW_Tactile_SPST_Angled_PTS645Vx58-2LFS001"
  Group = -> [Part__Feature122]
  Origin = -> Origin087
  Placement = pos=(89.1,-80,1.63) rot=(0,0,-1;1.5708rad)
FEATURE [Part::Feature] Part__Feature123  label="SOLID061"
FEATURE [App::Part] SFH4045N005
  Group = -> [Part__Feature123]
  Origin = -> Origin088
  Placement = pos=(90.3,-94,2.22) rot=(0.707107,0,0.707107;3.14159rad)
FEATURE [Part::Feature] Part__Feature124  label="SOLID062"
FEATURE [App::Part] R_0603_1608Metric005
  Group = -> [Part__Feature124]
  Origin = -> Origin089
  Placement = pos=(82.7,-97.1,1.63) rot=(0,0,1;1.5708rad)
FEATURE [Part::Feature] Part__Feature125  label="SOLID063"
FEATURE [App::Part] SFH4045N006
  Group = -> [Part__Feature125]
  Origin = -> Origin090
  Placement = pos=(85.6,-99.3,2.22) rot=(0.57735,-0.57735,0.57735;2.0944rad)
FEATURE [Part::Feature] Part__Feature126  label="COMPOUND006"
FEATURE [App::Part] FC68125003
  Group = -> [Part__Feature126]
  Origin = -> Origin091
  Placement = pos=(89.9,-49.65,1.63) rot=(0,0,1;1.5708rad)
FEATURE [Part::Feature] Part__Feature127  label="SOLID064"
FEATURE [App::Part] SOT_23_5  label="SOT-23-5"
  Group = -> [Part__Feature127]
  Origin = -> Origin092
  Placement = pos=(75.9375,-77.55,1.63) rot=(0,0,1;0rad)
FEATURE [Part::Feature] Part__Feature128  label="COMPOUND007"
FEATURE [App::Part] _90157000672004  label="690367280676"
  Group = -> [Part__Feature128]
  Origin = -> Origin093
  Placement = pos=(75.965,-84.05,4.13) rot=(0,0,1;0rad)
FEATURE [Part::Feature] Part__Feature129  label="SOLID065"
FEATURE [App::Part] SFH4045N007
  Group = -> [Part__Feature129]
  Origin = -> Origin094
  Placement = pos=(61.681,-93.2,2.22) rot=(0,-1,0;1.5708rad)
FEATURE [Part::Feature] Part__Feature130  label="SOLID066"
FEATURE [App::Part] Buzzer_Murata_PKMCS0909E4000_R002  label="Buzzer_Murata_PKMCS0909E4000-R002"
  Group = -> [Part__Feature130]
  Origin = -> Origin095
  Placement = pos=(76.3,-61.6,1.63) rot=(0,0,1;3.14159rad)
FEATURE [Part::Feature] Part__Feature131  label="SOLID067"
FEATURE [App::Part] SOT_024  label="SOT-024"
  Group = -> [Part__Feature131]
  Origin = -> Origin096
  Placement = pos=(86.4,-89.85,1.63) rot=(0,0,1;0rad)
FEATURE [Part::Feature] Part__Feature132  label="SOLID068"
FEATURE [App::Part] C_1210_3225Metric001
  Group = -> [Part__Feature132]
  Origin = -> Origin097
  Placement = pos=(82.8,-89.9,1.63) rot=(0,0,1;1.5708rad)
FEATURE [Part::Feature] Part__Feature133  label="SOLID069"
FEATURE [App::Part] PinSocket_1x04_P2_54mm_Vertical_SMD_Pin1Right001  label="PinSocket_1x04_P2.54mm_Vertical_SMD_Pin1Right001"
  Group = -> [Part__Feature133]
  Origin = -> Origin098
  Placement = pos=(76,-97.1,1.63) rot=(0,0,-1;1.5708rad)
FEATURE [Part::Feature] Part__Feature134  label="SOLID070"
FEATURE [App::Part] Vishay_MOLD_3Pin001  label="Vishay_MOLD-3Pin001"
  Group = -> [Part__Feature134]
  Origin = -> Origin099
  Placement = pos=(87.565,-73.74,1.63) rot=(0,0,1;1.5708rad)
FEATURE [Part::Feature] Part__Feature135  label="SOLID071"
FEATURE [App::Part] C_0603_1608Metric007
  Group = -> [Part__Feature135]
  Origin = -> Origin100
  Placement = pos=(72.8,-77.575,1.63) rot=(0,0,-1;1.5708rad)
FEATURE [Part::Feature] Part__Feature136  label="SOLID072"
FEATURE [App::Part] C_0603_1608Metric008
  Group = -> [Part__Feature136]
  Origin = -> Origin101
  Placement = pos=(79.1,-77.6,1.63) rot=(0,0,-1;1.5708rad)
FEATURE [Part::Feature] Part__Feature137  label="SOLID073"
FEATURE [App::Part] C_0603_1608Metric009
  Group = -> [Part__Feature137]
  Origin = -> Origin102
  Placement = pos=(80.9,-77.6,1.63) rot=(0,0,-1;1.5708rad)
FEATURE [Part::Feature] Part__Feature138  label="COMPOUND008"
FEATURE [App::Part] ArduinoNanoRP2041
  Group = -> [Part__Feature138]
  Origin = -> Origin103
  Placement = pos=(73.4,-78.1,-0.05) rot=(0,0.707107,-0.707107;3.14159rad)
FEATURE [Part::Feature] Part__Feature139  label="FM3_mainboard PCB001"
FEATURE [App::Part] FM3_mainboard_002  label="FM3_mainboard 002"
  Group = -> [C_0603_1608Metric004,SFH4045N004,D_SOD_323002,R_0603_1608Metric003,FC68125002,C_0603_1608Metric005,C_0603_1608Metric006,D_SOD_323003,R_0603_1608Metric004,SW_Tactile_SPST_Angled_PTS645Vx58_2LFS001,SFH4045N005,R_0603_1608Metric005,SFH4045N006,FC68125003,SOT_23_5,_90157000672004,SFH4045N007,Buzzer_Murata_PKMCS0909E4000_R002,SOT_024,C_1210_3225Metric001,+7 more]
  Origin = -> Origin104
FEATURE [App::VRMLObject] FM3_mainboard
